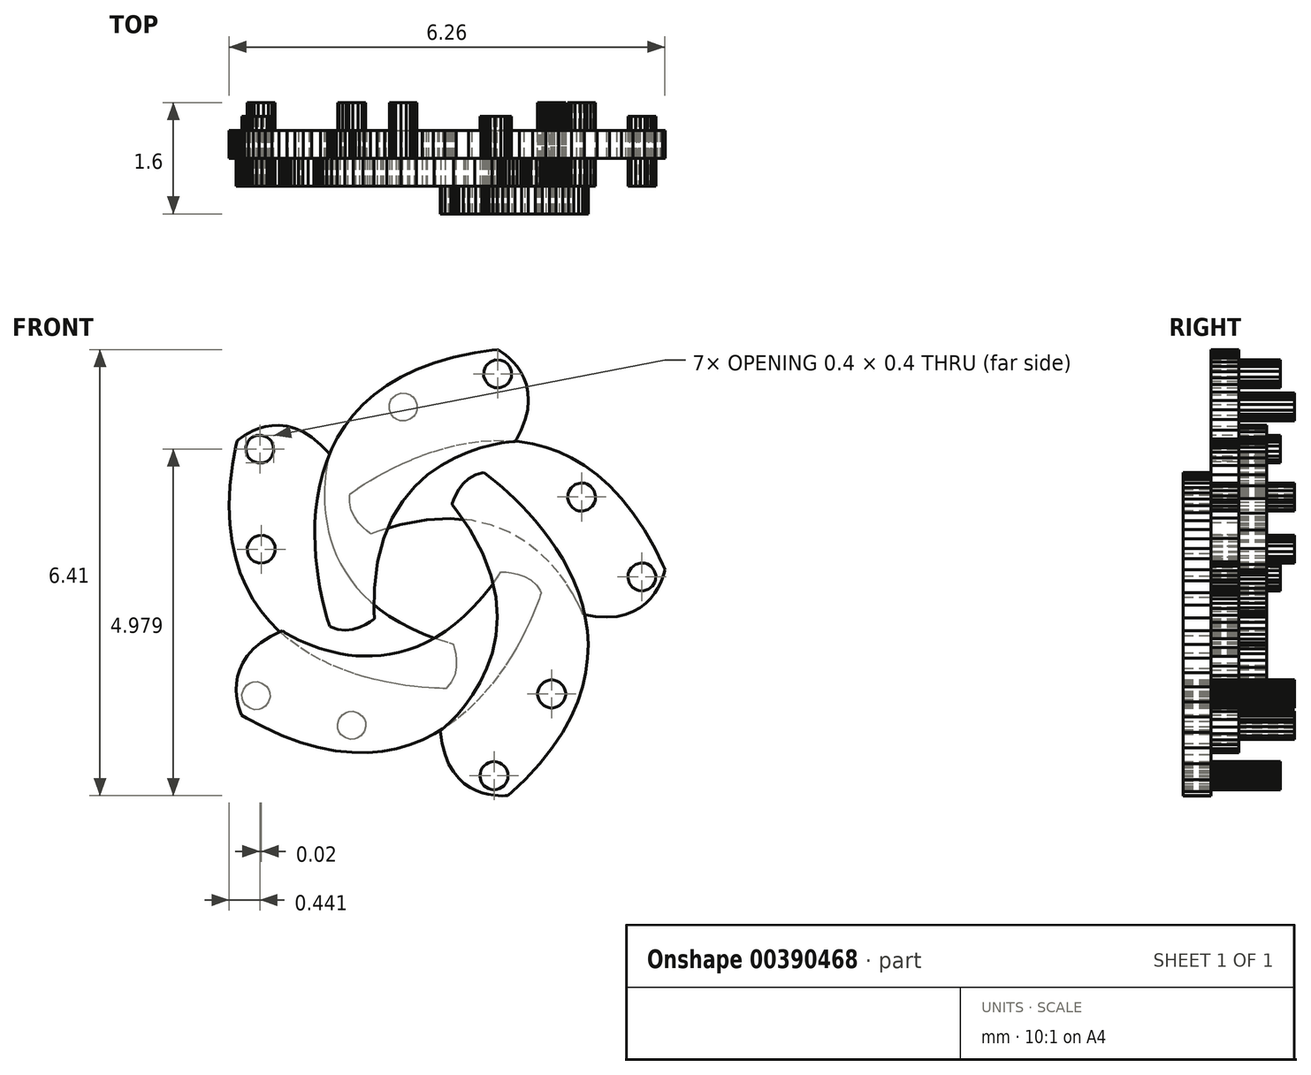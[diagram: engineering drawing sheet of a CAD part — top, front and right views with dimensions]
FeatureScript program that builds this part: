
annotation { "Feature Type Name" : "Feature", "Feature Type Description" : "" }
export const myFeature = defineFeature(function(context is Context, id is Id, definition is map)
    precondition{}
    {
        {
            var Q0;
            Q0=qCreatedBy(makeId("Front.planeOp"),FACE);
            var sketch = newSketch(context, id + "F0", { "sketchPlane" : qUnion([Q0])});
            skLineSegment(sketch, "E0", {"start": v(0.33, 0.98) * mm, "end": v(0.34, 1) * mm});
            skLineSegment(sketch, "E1", {"start": v(0.34, 1) * mm, "end": v(0.36, 1.05) * mm});
            skLineSegment(sketch, "E2", {"start": v(0.36, 1.05) * mm, "end": v(0.39, 1.12) * mm});
            skLineSegment(sketch, "E3", {"start": v(0.39, 1.12) * mm, "end": v(0.43, 1.2) * mm});
            skLineSegment(sketch, "E4", {"start": v(0.43, 1.2) * mm, "end": v(0.5, 1.28) * mm});
            skLineSegment(sketch, "E5", {"start": v(0.5, 1.28) * mm, "end": v(0.57, 1.36) * mm});
            skLineSegment(sketch, "E6", {"start": v(0.57, 1.36) * mm, "end": v(0.67, 1.41) * mm});
            skLineSegment(sketch, "E7", {"start": v(0.67, 1.41) * mm, "end": v(0.76, 1.44) * mm});
            skLineSegment(sketch, "E8", {"start": v(0.76, 1.44) * mm, "end": v(0.8, 1.44) * mm});
            skLineSegment(sketch, "E9", {"start": v(0.8, 1.44) * mm, "end": v(0.8, 1.43) * mm});
            skLineSegment(sketch, "E10", {"start": v(0.8, 1.43) * mm, "end": v(0.83, 1.42) * mm});
            skLineSegment(sketch, "E11", {"start": v(0.83, 1.42) * mm, "end": v(0.87, 1.38) * mm});
            skLineSegment(sketch, "E12", {"start": v(0.87, 1.38) * mm, "end": v(0.92, 1.34) * mm});
            skLineSegment(sketch, "E13", {"start": v(0.92, 1.34) * mm, "end": v(0.99, 1.29) * mm});
            skLineSegment(sketch, "E14", {"start": v(0.99, 1.29) * mm, "end": v(1.06, 1.22) * mm});
            skLineSegment(sketch, "E15", {"start": v(1.06, 1.22) * mm, "end": v(1.15, 1.15) * mm});
            skLineSegment(sketch, "E16", {"start": v(1.15, 1.15) * mm, "end": v(1.24, 1.06) * mm});
            skLineSegment(sketch, "E17", {"start": v(1.24, 1.06) * mm, "end": v(1.33, 0.97) * mm});
            skLineSegment(sketch, "E18", {"start": v(1.33, 0.97) * mm, "end": v(1.43, 0.86) * mm});
            skLineSegment(sketch, "E19", {"start": v(1.43, 0.86) * mm, "end": v(1.53, 0.75) * mm});
            skLineSegment(sketch, "E20", {"start": v(1.53, 0.75) * mm, "end": v(1.63, 0.62) * mm});
            skLineSegment(sketch, "E21", {"start": v(1.63, 0.62) * mm, "end": v(1.73, 0.5) * mm});
            skLineSegment(sketch, "E22", {"start": v(1.73, 0.5) * mm, "end": v(1.83, 0.35) * mm});
            skLineSegment(sketch, "E23", {"start": v(1.83, 0.35) * mm, "end": v(1.92, 0.2) * mm});
            skLineSegment(sketch, "E24", {"start": v(1.92, 0.2) * mm, "end": v(2, 0.05) * mm});
            skLineSegment(sketch, "E25", {"start": v(2, 0.05) * mm, "end": v(2.08, -0.12) * mm});
            skLineSegment(sketch, "E26", {"start": v(2.08, -0.12) * mm, "end": v(2.15, -0.29) * mm});
            skLineSegment(sketch, "E27", {"start": v(2.15, -0.29) * mm, "end": v(2.2, -0.46) * mm});
            skLineSegment(sketch, "E28", {"start": v(2.2, -0.46) * mm, "end": v(2.25, -0.64) * mm});
            skLineSegment(sketch, "E29", {"start": v(2.25, -0.64) * mm, "end": v(2.28, -0.83) * mm});
            skLineSegment(sketch, "E30", {"start": v(2.28, -0.83) * mm, "end": v(2.29, -1.03) * mm});
            skLineSegment(sketch, "E31", {"start": v(2.29, -1.03) * mm, "end": v(2.28, -1.23) * mm});
            skLineSegment(sketch, "E32", {"start": v(2.28, -1.23) * mm, "end": v(2.26, -1.43) * mm});
            skLineSegment(sketch, "E33", {"start": v(2.26, -1.43) * mm, "end": v(2.2, -1.64) * mm});
            skLineSegment(sketch, "E34", {"start": v(2.2, -1.64) * mm, "end": v(2.14, -1.85) * mm});
            skLineSegment(sketch, "E35", {"start": v(2.14, -1.85) * mm, "end": v(2.04, -2.07) * mm});
            skLineSegment(sketch, "E36", {"start": v(2.04, -2.07) * mm, "end": v(1.92, -2.29) * mm});
            skLineSegment(sketch, "E37", {"start": v(1.92, -2.29) * mm, "end": v(1.77, -2.51) * mm});
            skLineSegment(sketch, "E38", {"start": v(1.77, -2.51) * mm, "end": v(1.6, -2.74) * mm});
            skLineSegment(sketch, "E39", {"start": v(1.6, -2.74) * mm, "end": v(1.38, -2.97) * mm});
            skLineSegment(sketch, "E40", {"start": v(1.38, -2.97) * mm, "end": v(1.2, -3.14) * mm});
            skLineSegment(sketch, "E41", {"start": v(1.2, -3.14) * mm, "end": v(1.14, -3.2) * mm});
            skLineSegment(sketch, "E42", {"start": v(1.14, -3.2) * mm, "end": v(1.13, -3.2) * mm});
            skLineSegment(sketch, "E43", {"start": v(1.13, -3.2) * mm, "end": v(1.1, -3.2) * mm});
            skLineSegment(sketch, "E44", {"start": v(1.1, -3.2) * mm, "end": v(1.06, -3.2) * mm});
            skLineSegment(sketch, "E45", {"start": v(1.06, -3.2) * mm, "end": v(1, -3.2) * mm});
            skLineSegment(sketch, "E46", {"start": v(1, -3.2) * mm, "end": v(0.93, -3.2) * mm});
            skLineSegment(sketch, "E47", {"start": v(0.93, -3.2) * mm, "end": v(0.85, -3.18) * mm});
            skLineSegment(sketch, "E48", {"start": v(0.85, -3.18) * mm, "end": v(0.77, -3.16) * mm});
            skLineSegment(sketch, "E49", {"start": v(0.77, -3.16) * mm, "end": v(0.68, -3.13) * mm});
            skLineSegment(sketch, "E50", {"start": v(0.68, -3.13) * mm, "end": v(0.6, -3.09) * mm});
            skLineSegment(sketch, "E51", {"start": v(0.6, -3.09) * mm, "end": v(0.51, -3.03) * mm});
            skLineSegment(sketch, "E52", {"start": v(0.51, -3.03) * mm, "end": v(0.43, -2.95) * mm});
            skLineSegment(sketch, "E53", {"start": v(0.43, -2.95) * mm, "end": v(0.35, -2.86) * mm});
            skLineSegment(sketch, "E54", {"start": v(0.35, -2.86) * mm, "end": v(0.29, -2.75) * mm});
            skLineSegment(sketch, "E55", {"start": v(0.29, -2.75) * mm, "end": v(0.23, -2.61) * mm});
            skLineSegment(sketch, "E56", {"start": v(0.23, -2.61) * mm, "end": v(0.2, -2.45) * mm});
            skLineSegment(sketch, "E57", {"start": v(0.2, -2.45) * mm, "end": v(0.17, -2.31) * mm});
            skLineSegment(sketch, "E58", {"start": v(0.17, -2.31) * mm, "end": v(0.17, -2.27) * mm});
            skLineSegment(sketch, "E59", {"start": v(0.17, -2.27) * mm, "end": v(0.19, -2.25) * mm});
            skLineSegment(sketch, "E60", {"start": v(0.19, -2.25) * mm, "end": v(0.24, -2.2) * mm});
            skLineSegment(sketch, "E61", {"start": v(0.24, -2.2) * mm, "end": v(0.32, -2.14) * mm});
            skLineSegment(sketch, "E62", {"start": v(0.32, -2.14) * mm, "end": v(0.41, -2.03) * mm});
            skLineSegment(sketch, "E63", {"start": v(0.41, -2.03) * mm, "end": v(0.52, -1.9) * mm});
            skLineSegment(sketch, "E64", {"start": v(0.52, -1.9) * mm, "end": v(0.63, -1.75) * mm});
            skLineSegment(sketch, "E65", {"start": v(0.63, -1.75) * mm, "end": v(0.74, -1.57) * mm});
            skLineSegment(sketch, "E66", {"start": v(0.74, -1.57) * mm, "end": v(0.83, -1.37) * mm});
            skLineSegment(sketch, "E67", {"start": v(0.83, -1.37) * mm, "end": v(0.91, -1.15) * mm});
            skLineSegment(sketch, "E68", {"start": v(0.91, -1.15) * mm, "end": v(0.96, -0.9) * mm});
            skLineSegment(sketch, "E69", {"start": v(0.96, -0.9) * mm, "end": v(0.98, -0.63) * mm});
            skLineSegment(sketch, "E70", {"start": v(0.98, -0.63) * mm, "end": v(0.96, -0.35) * mm});
            skLineSegment(sketch, "E71", {"start": v(0.96, -0.35) * mm, "end": v(0.9, -0.04) * mm});
            skLineSegment(sketch, "E72", {"start": v(0.9, -0.04) * mm, "end": v(0.77, 0.28) * mm});
            skLineSegment(sketch, "E73", {"start": v(0.77, 0.28) * mm, "end": v(0.59, 0.62) * mm});
            skLineSegment(sketch, "E74", {"start": v(0.59, 0.62) * mm, "end": v(0.4, 0.9) * mm});
            skLineSegment(sketch, "E75", {"start": v(0.4, 0.9) * mm, "end": v(0.33, 0.98) * mm});
            skLineSegment(sketch, "E76", {"start": v(1.14, -2.91) * mm, "end": v(1.14, -2.92) * mm});
            skLineSegment(sketch, "E77", {"start": v(1.14, -2.92) * mm, "end": v(1.13, -2.95) * mm});
            skLineSegment(sketch, "E78", {"start": v(1.13, -2.95) * mm, "end": v(1.12, -3) * mm});
            skLineSegment(sketch, "E79", {"start": v(1.12, -3) * mm, "end": v(1.1, -3.03) * mm});
            skLineSegment(sketch, "E80", {"start": v(1.1, -3.03) * mm, "end": v(1.08, -3.06) * mm});
            skLineSegment(sketch, "E81", {"start": v(1.08, -3.06) * mm, "end": v(1.05, -3.08) * mm});
            skLineSegment(sketch, "E82", {"start": v(1.05, -3.08) * mm, "end": v(1.02, -3.1) * mm});
            skLineSegment(sketch, "E83", {"start": v(1.02, -3.1) * mm, "end": v(0.98, -3.11) * mm});
            skLineSegment(sketch, "E84", {"start": v(0.98, -3.11) * mm, "end": v(0.95, -3.12) * mm});
            skLineSegment(sketch, "E85", {"start": v(0.95, -3.12) * mm, "end": v(0.94, -3.12) * mm});
            skLineSegment(sketch, "E86", {"start": v(0.94, -3.12) * mm, "end": v(0.93, -3.12) * mm});
            skLineSegment(sketch, "E87", {"start": v(0.93, -3.12) * mm, "end": v(0.9, -3.11) * mm});
            skLineSegment(sketch, "E88", {"start": v(0.9, -3.11) * mm, "end": v(0.86, -3.1) * mm});
            skLineSegment(sketch, "E89", {"start": v(0.86, -3.1) * mm, "end": v(0.82, -3.08) * mm});
            skLineSegment(sketch, "E90", {"start": v(0.82, -3.08) * mm, "end": v(0.8, -3.06) * mm});
            skLineSegment(sketch, "E91", {"start": v(0.8, -3.06) * mm, "end": v(0.77, -3.03) * mm});
            skLineSegment(sketch, "E92", {"start": v(0.77, -3.03) * mm, "end": v(0.75, -3) * mm});
            skLineSegment(sketch, "E93", {"start": v(0.75, -3) * mm, "end": v(0.74, -2.95) * mm});
            skLineSegment(sketch, "E94", {"start": v(0.74, -2.95) * mm, "end": v(0.74, -2.92) * mm});
            skLineSegment(sketch, "E95", {"start": v(0.74, -2.92) * mm, "end": v(0.74, -2.91) * mm});
            skLineSegment(sketch, "E96", {"start": v(0.74, -2.91) * mm, "end": v(0.74, -2.9) * mm});
            skLineSegment(sketch, "E97", {"start": v(0.74, -2.9) * mm, "end": v(0.74, -2.87) * mm});
            skLineSegment(sketch, "E98", {"start": v(0.74, -2.87) * mm, "end": v(0.75, -2.84) * mm});
            skLineSegment(sketch, "E99", {"start": v(0.75, -2.84) * mm, "end": v(0.77, -2.8) * mm});
            skLineSegment(sketch, "E100", {"start": v(0.77, -2.8) * mm, "end": v(0.8, -2.77) * mm});
            skLineSegment(sketch, "E101", {"start": v(0.8, -2.77) * mm, "end": v(0.82, -2.75) * mm});
            skLineSegment(sketch, "E102", {"start": v(0.82, -2.75) * mm, "end": v(0.86, -2.73) * mm});
            skLineSegment(sketch, "E103", {"start": v(0.86, -2.73) * mm, "end": v(0.9, -2.72) * mm});
            skLineSegment(sketch, "E104", {"start": v(0.9, -2.72) * mm, "end": v(0.93, -2.71) * mm});
            skLineSegment(sketch, "E105", {"start": v(0.93, -2.71) * mm, "end": v(0.94, -2.71) * mm});
            skLineSegment(sketch, "E106", {"start": v(0.94, -2.71) * mm, "end": v(0.95, -2.71) * mm});
            skLineSegment(sketch, "E107", {"start": v(0.95, -2.71) * mm, "end": v(0.98, -2.72) * mm});
            skLineSegment(sketch, "E108", {"start": v(0.98, -2.72) * mm, "end": v(1.02, -2.73) * mm});
            skLineSegment(sketch, "E109", {"start": v(1.02, -2.73) * mm, "end": v(1.05, -2.75) * mm});
            skLineSegment(sketch, "E110", {"start": v(1.05, -2.75) * mm, "end": v(1.08, -2.77) * mm});
            skLineSegment(sketch, "E111", {"start": v(1.08, -2.77) * mm, "end": v(1.1, -2.8) * mm});
            skLineSegment(sketch, "E112", {"start": v(1.1, -2.8) * mm, "end": v(1.12, -2.84) * mm});
            skLineSegment(sketch, "E113", {"start": v(1.12, -2.84) * mm, "end": v(1.13, -2.87) * mm});
            skLineSegment(sketch, "E114", {"start": v(1.13, -2.87) * mm, "end": v(1.14, -2.9) * mm});
            skLineSegment(sketch, "E115", {"start": v(1.14, -2.9) * mm, "end": v(1.14, -2.91) * mm});
            skLineSegment(sketch, "E116", {"start": v(1.97, -1.74) * mm, "end": v(1.97, -1.75) * mm});
            skLineSegment(sketch, "E117", {"start": v(1.97, -1.75) * mm, "end": v(1.96, -1.78) * mm});
            skLineSegment(sketch, "E118", {"start": v(1.96, -1.78) * mm, "end": v(1.95, -1.82) * mm});
            skLineSegment(sketch, "E119", {"start": v(1.95, -1.82) * mm, "end": v(1.93, -1.85) * mm});
            skLineSegment(sketch, "E120", {"start": v(1.93, -1.85) * mm, "end": v(1.9, -1.88) * mm});
            skLineSegment(sketch, "E121", {"start": v(1.9, -1.88) * mm, "end": v(1.88, -1.9) * mm});
            skLineSegment(sketch, "E122", {"start": v(1.88, -1.9) * mm, "end": v(1.84, -1.92) * mm});
            skLineSegment(sketch, "E123", {"start": v(1.84, -1.92) * mm, "end": v(1.8, -1.94) * mm});
            skLineSegment(sketch, "E124", {"start": v(1.8, -1.94) * mm, "end": v(1.78, -1.94) * mm});
            skLineSegment(sketch, "E125", {"start": v(1.78, -1.94) * mm, "end": v(1.77, -1.94) * mm});
            skLineSegment(sketch, "E126", {"start": v(1.77, -1.94) * mm, "end": v(1.76, -1.94) * mm});
            skLineSegment(sketch, "E127", {"start": v(1.76, -1.94) * mm, "end": v(1.72, -1.94) * mm});
            skLineSegment(sketch, "E128", {"start": v(1.72, -1.94) * mm, "end": v(1.69, -1.92) * mm});
            skLineSegment(sketch, "E129", {"start": v(1.69, -1.92) * mm, "end": v(1.65, -1.9) * mm});
            skLineSegment(sketch, "E130", {"start": v(1.65, -1.9) * mm, "end": v(1.62, -1.88) * mm});
            skLineSegment(sketch, "E131", {"start": v(1.62, -1.88) * mm, "end": v(1.6, -1.85) * mm});
            skLineSegment(sketch, "E132", {"start": v(1.6, -1.85) * mm, "end": v(1.58, -1.82) * mm});
            skLineSegment(sketch, "E133", {"start": v(1.58, -1.82) * mm, "end": v(1.57, -1.78) * mm});
            skLineSegment(sketch, "E134", {"start": v(1.57, -1.78) * mm, "end": v(1.56, -1.75) * mm});
            skLineSegment(sketch, "E135", {"start": v(1.56, -1.75) * mm, "end": v(1.56, -1.74) * mm});
            skLineSegment(sketch, "E136", {"start": v(1.56, -1.74) * mm, "end": v(1.56, -1.73) * mm});
            skLineSegment(sketch, "E137", {"start": v(1.56, -1.73) * mm, "end": v(1.57, -1.7) * mm});
            skLineSegment(sketch, "E138", {"start": v(1.57, -1.7) * mm, "end": v(1.58, -1.66) * mm});
            skLineSegment(sketch, "E139", {"start": v(1.58, -1.66) * mm, "end": v(1.6, -1.63) * mm});
            skLineSegment(sketch, "E140", {"start": v(1.6, -1.63) * mm, "end": v(1.62, -1.6) * mm});
            skLineSegment(sketch, "E141", {"start": v(1.62, -1.6) * mm, "end": v(1.65, -1.57) * mm});
            skLineSegment(sketch, "E142", {"start": v(1.65, -1.57) * mm, "end": v(1.69, -1.55) * mm});
            skLineSegment(sketch, "E143", {"start": v(1.69, -1.55) * mm, "end": v(1.72, -1.54) * mm});
            skLineSegment(sketch, "E144", {"start": v(1.72, -1.54) * mm, "end": v(1.76, -1.54) * mm});
            skLineSegment(sketch, "E145", {"start": v(1.76, -1.54) * mm, "end": v(1.77, -1.54) * mm});
            skLineSegment(sketch, "E146", {"start": v(1.77, -1.54) * mm, "end": v(1.78, -1.54) * mm});
            skLineSegment(sketch, "E147", {"start": v(1.78, -1.54) * mm, "end": v(1.8, -1.54) * mm});
            skLineSegment(sketch, "E148", {"start": v(1.8, -1.54) * mm, "end": v(1.84, -1.55) * mm});
            skLineSegment(sketch, "E149", {"start": v(1.84, -1.55) * mm, "end": v(1.88, -1.57) * mm});
            skLineSegment(sketch, "E150", {"start": v(1.88, -1.57) * mm, "end": v(1.9, -1.6) * mm});
            skLineSegment(sketch, "E151", {"start": v(1.9, -1.6) * mm, "end": v(1.93, -1.63) * mm});
            skLineSegment(sketch, "E152", {"start": v(1.93, -1.63) * mm, "end": v(1.95, -1.66) * mm});
            skLineSegment(sketch, "E153", {"start": v(1.95, -1.66) * mm, "end": v(1.96, -1.7) * mm});
            skLineSegment(sketch, "E154", {"start": v(1.96, -1.7) * mm, "end": v(1.97, -1.73) * mm});
            skLineSegment(sketch, "E155", {"start": v(1.97, -1.73) * mm, "end": v(1.97, -1.74) * mm});
            skLineSegment(sketch, "E156", {"start": v(-0.83, 0.56) * mm, "end": v(-0.85, 0.57) * mm});
            skLineSegment(sketch, "E157", {"start": v(-0.85, 0.57) * mm, "end": v(-0.89, 0.6) * mm});
            skLineSegment(sketch, "E158", {"start": v(-0.89, 0.6) * mm, "end": v(-0.95, 0.65) * mm});
            skLineSegment(sketch, "E159", {"start": v(-0.95, 0.65) * mm, "end": v(-1, 0.72) * mm});
            skLineSegment(sketch, "E160", {"start": v(-1, 0.72) * mm, "end": v(-1.07, 0.8) * mm});
            skLineSegment(sketch, "E161", {"start": v(-1.07, 0.8) * mm, "end": v(-1.12, 0.9) * mm});
            skLineSegment(sketch, "E162", {"start": v(-1.12, 0.9) * mm, "end": v(-1.14, 1.02) * mm});
            skLineSegment(sketch, "E163", {"start": v(-1.14, 1.02) * mm, "end": v(-1.13, 1.1) * mm});
            skLineSegment(sketch, "E164", {"start": v(-1.13, 1.1) * mm, "end": v(-1.13, 1.14) * mm});
            skLineSegment(sketch, "E165", {"start": v(-1.13, 1.14) * mm, "end": v(-1.12, 1.14) * mm});
            skLineSegment(sketch, "E166", {"start": v(-1.12, 1.14) * mm, "end": v(-1.1, 1.16) * mm});
            skLineSegment(sketch, "E167", {"start": v(-1.1, 1.16) * mm, "end": v(-1.05, 1.2) * mm});
            skLineSegment(sketch, "E168", {"start": v(-1.05, 1.2) * mm, "end": v(-1, 1.23) * mm});
            skLineSegment(sketch, "E169", {"start": v(-1, 1.23) * mm, "end": v(-0.92, 1.28) * mm});
            skLineSegment(sketch, "E170", {"start": v(-0.92, 1.28) * mm, "end": v(-0.84, 1.33) * mm});
            skLineSegment(sketch, "E171", {"start": v(-0.84, 1.33) * mm, "end": v(-0.74, 1.39) * mm});
            skLineSegment(sketch, "E172", {"start": v(-0.74, 1.39) * mm, "end": v(-0.63, 1.45) * mm});
            skLineSegment(sketch, "E173", {"start": v(-0.63, 1.45) * mm, "end": v(-0.51, 1.5) * mm});
            skLineSegment(sketch, "E174", {"start": v(-0.51, 1.5) * mm, "end": v(-0.38, 1.57) * mm});
            skLineSegment(sketch, "E175", {"start": v(-0.38, 1.57) * mm, "end": v(-0.24, 1.63) * mm});
            skLineSegment(sketch, "E176", {"start": v(-0.24, 1.63) * mm, "end": v(-0.1, 1.69) * mm});
            skLineSegment(sketch, "E177", {"start": v(-0.1, 1.69) * mm, "end": v(0.06, 1.74) * mm});
            skLineSegment(sketch, "E178", {"start": v(0.06, 1.74) * mm, "end": v(0.23, 1.8) * mm});
            skLineSegment(sketch, "E179", {"start": v(0.23, 1.8) * mm, "end": v(0.4, 1.83) * mm});
            skLineSegment(sketch, "E180", {"start": v(0.4, 1.83) * mm, "end": v(0.57, 1.87) * mm});
            skLineSegment(sketch, "E181", {"start": v(0.57, 1.87) * mm, "end": v(0.75, 1.9) * mm});
            skLineSegment(sketch, "E182", {"start": v(0.75, 1.9) * mm, "end": v(0.93, 1.9) * mm});
            skLineSegment(sketch, "E183", {"start": v(0.93, 1.9) * mm, "end": v(1.12, 1.9) * mm});
            skLineSegment(sketch, "E184", {"start": v(1.12, 1.9) * mm, "end": v(1.3, 1.89) * mm});
            skLineSegment(sketch, "E185", {"start": v(1.3, 1.89) * mm, "end": v(1.5, 1.86) * mm});
            skLineSegment(sketch, "E186", {"start": v(1.5, 1.86) * mm, "end": v(1.68, 1.8) * mm});
            skLineSegment(sketch, "E187", {"start": v(1.68, 1.8) * mm, "end": v(1.87, 1.74) * mm});
            skLineSegment(sketch, "E188", {"start": v(1.87, 1.74) * mm, "end": v(2.05, 1.65) * mm});
            skLineSegment(sketch, "E189", {"start": v(2.05, 1.65) * mm, "end": v(2.24, 1.54) * mm});
            skLineSegment(sketch, "E190", {"start": v(2.24, 1.54) * mm, "end": v(2.42, 1.41) * mm});
            skLineSegment(sketch, "E191", {"start": v(2.42, 1.41) * mm, "end": v(2.6, 1.25) * mm});
            skLineSegment(sketch, "E192", {"start": v(2.6, 1.25) * mm, "end": v(2.77, 1.07) * mm});
            skLineSegment(sketch, "E193", {"start": v(2.77, 1.07) * mm, "end": v(2.94, 0.86) * mm});
            skLineSegment(sketch, "E194", {"start": v(2.94, 0.86) * mm, "end": v(3.1, 0.62) * mm});
            skLineSegment(sketch, "E195", {"start": v(3.1, 0.62) * mm, "end": v(3.25, 0.35) * mm});
            skLineSegment(sketch, "E196", {"start": v(3.25, 0.35) * mm, "end": v(3.36, 0.12) * mm});
            skLineSegment(sketch, "E197", {"start": v(3.36, 0.12) * mm, "end": v(3.4, 0.05) * mm});
            skLineSegment(sketch, "E198", {"start": v(3.4, 0.05) * mm, "end": v(3.4, 0.04) * mm});
            skLineSegment(sketch, "E199", {"start": v(3.4, 0.04) * mm, "end": v(3.39, 0) * mm});
            skLineSegment(sketch, "E200", {"start": v(3.39, 0) * mm, "end": v(3.37, -0.03) * mm});
            skLineSegment(sketch, "E201", {"start": v(3.37, -0.03) * mm, "end": v(3.35, -0.09) * mm});
            skLineSegment(sketch, "E202", {"start": v(3.35, -0.09) * mm, "end": v(3.33, -0.15) * mm});
            skLineSegment(sketch, "E203", {"start": v(3.33, -0.15) * mm, "end": v(3.3, -0.22) * mm});
            skLineSegment(sketch, "E204", {"start": v(3.3, -0.22) * mm, "end": v(3.25, -0.3) * mm});
            skLineSegment(sketch, "E205", {"start": v(3.25, -0.3) * mm, "end": v(3.19, -0.36) * mm});
            skLineSegment(sketch, "E206", {"start": v(3.19, -0.36) * mm, "end": v(3.12, -0.43) * mm});
            skLineSegment(sketch, "E207", {"start": v(3.12, -0.43) * mm, "end": v(3.04, -0.5) * mm});
            skLineSegment(sketch, "E208", {"start": v(3.04, -0.5) * mm, "end": v(2.94, -0.55) * mm});
            skLineSegment(sketch, "E209", {"start": v(2.94, -0.55) * mm, "end": v(2.83, -0.6) * mm});
            skLineSegment(sketch, "E210", {"start": v(2.83, -0.6) * mm, "end": v(2.7, -0.62) * mm});
            skLineSegment(sketch, "E211", {"start": v(2.7, -0.62) * mm, "end": v(2.56, -0.64) * mm});
            skLineSegment(sketch, "E212", {"start": v(2.56, -0.64) * mm, "end": v(2.4, -0.63) * mm});
            skLineSegment(sketch, "E213", {"start": v(2.4, -0.63) * mm, "end": v(2.26, -0.6) * mm});
            skLineSegment(sketch, "E214", {"start": v(2.26, -0.6) * mm, "end": v(2.21, -0.6) * mm});
            skLineSegment(sketch, "E215", {"start": v(2.21, -0.6) * mm, "end": v(2.2, -0.57) * mm});
            skLineSegment(sketch, "E216", {"start": v(2.2, -0.57) * mm, "end": v(2.18, -0.5) * mm});
            skLineSegment(sketch, "E217", {"start": v(2.18, -0.5) * mm, "end": v(2.13, -0.41) * mm});
            skLineSegment(sketch, "E218", {"start": v(2.13, -0.41) * mm, "end": v(2.06, -0.29) * mm});
            skLineSegment(sketch, "E219", {"start": v(2.06, -0.29) * mm, "end": v(1.97, -0.15) * mm});
            skLineSegment(sketch, "E220", {"start": v(1.97, -0.15) * mm, "end": v(1.86, 0) * mm});
            skLineSegment(sketch, "E221", {"start": v(1.86, 0) * mm, "end": v(1.72, 0.16) * mm});
            skLineSegment(sketch, "E222", {"start": v(1.72, 0.16) * mm, "end": v(1.56, 0.32) * mm});
            skLineSegment(sketch, "E223", {"start": v(1.56, 0.32) * mm, "end": v(1.37, 0.46) * mm});
            skLineSegment(sketch, "E224", {"start": v(1.37, 0.46) * mm, "end": v(1.15, 0.58) * mm});
            skLineSegment(sketch, "E225", {"start": v(1.15, 0.58) * mm, "end": v(0.9, 0.69) * mm});
            skLineSegment(sketch, "E226", {"start": v(0.9, 0.69) * mm, "end": v(0.63, 0.75) * mm});
            skLineSegment(sketch, "E227", {"start": v(0.63, 0.75) * mm, "end": v(0.31, 0.78) * mm});
            skLineSegment(sketch, "E228", {"start": v(0.31, 0.78) * mm, "end": v(-0.03, 0.77) * mm});
            skLineSegment(sketch, "E229", {"start": v(-0.03, 0.77) * mm, "end": v(-0.41, 0.7) * mm});
            skLineSegment(sketch, "E230", {"start": v(-0.41, 0.7) * mm, "end": v(-0.73, 0.6) * mm});
            skLineSegment(sketch, "E231", {"start": v(-0.73, 0.6) * mm, "end": v(-0.83, 0.56) * mm});
            skLineSegment(sketch, "E232", {"start": v(3.12, 0.13) * mm, "end": v(3.14, 0.13) * mm});
            skLineSegment(sketch, "E233", {"start": v(3.14, 0.13) * mm, "end": v(3.2, 0.1) * mm});
            skLineSegment(sketch, "E234", {"start": v(3.2, 0.1) * mm, "end": v(3.24, 0.03) * mm});
            skLineSegment(sketch, "E235", {"start": v(3.24, 0.03) * mm, "end": v(3.26, -0.04) * mm});
            skLineSegment(sketch, "E236", {"start": v(3.26, -0.04) * mm, "end": v(3.26, -0.1) * mm});
            skLineSegment(sketch, "E237", {"start": v(3.26, -0.1) * mm, "end": v(3.25, -0.12) * mm});
            skLineSegment(sketch, "E238", {"start": v(3.25, -0.12) * mm, "end": v(3.25, -0.14) * mm});
            skLineSegment(sketch, "E239", {"start": v(3.25, -0.14) * mm, "end": v(3.21, -0.19) * mm});
            skLineSegment(sketch, "E240", {"start": v(3.21, -0.19) * mm, "end": v(3.15, -0.24) * mm});
            skLineSegment(sketch, "E241", {"start": v(3.15, -0.24) * mm, "end": v(3.08, -0.26) * mm});
            skLineSegment(sketch, "E242", {"start": v(3.08, -0.26) * mm, "end": v(3.02, -0.26) * mm});
            skLineSegment(sketch, "E243", {"start": v(3.02, -0.26) * mm, "end": v(3, -0.25) * mm});
            skLineSegment(sketch, "E244", {"start": v(3, -0.25) * mm, "end": v(2.98, -0.24) * mm});
            skLineSegment(sketch, "E245", {"start": v(2.98, -0.24) * mm, "end": v(2.93, -0.21) * mm});
            skLineSegment(sketch, "E246", {"start": v(2.93, -0.21) * mm, "end": v(2.88, -0.15) * mm});
            skLineSegment(sketch, "E247", {"start": v(2.88, -0.15) * mm, "end": v(2.86, -0.08) * mm});
            skLineSegment(sketch, "E248", {"start": v(2.86, -0.08) * mm, "end": v(2.86, -0.01) * mm});
            skLineSegment(sketch, "E249", {"start": v(2.86, -0.01) * mm, "end": v(2.87, 0) * mm});
            skLineSegment(sketch, "E250", {"start": v(2.87, 0) * mm, "end": v(2.88, 0.02) * mm});
            skLineSegment(sketch, "E251", {"start": v(2.88, 0.02) * mm, "end": v(2.9, 0.07) * mm});
            skLineSegment(sketch, "E252", {"start": v(2.9, 0.07) * mm, "end": v(2.97, 0.12) * mm});
            skLineSegment(sketch, "E253", {"start": v(2.97, 0.12) * mm, "end": v(3.04, 0.14) * mm});
            skLineSegment(sketch, "E254", {"start": v(3.04, 0.14) * mm, "end": v(3.1, 0.14) * mm});
            skLineSegment(sketch, "E255", {"start": v(3.1, 0.14) * mm, "end": v(3.12, 0.13) * mm});
            skLineSegment(sketch, "E256", {"start": v(2.26, 1.28) * mm, "end": v(2.28, 1.28) * mm});
            skLineSegment(sketch, "E257", {"start": v(2.28, 1.28) * mm, "end": v(2.33, 1.24) * mm});
            skLineSegment(sketch, "E258", {"start": v(2.33, 1.24) * mm, "end": v(2.37, 1.18) * mm});
            skLineSegment(sketch, "E259", {"start": v(2.37, 1.18) * mm, "end": v(2.4, 1.1) * mm});
            skLineSegment(sketch, "E260", {"start": v(2.4, 1.1) * mm, "end": v(2.4, 1.05) * mm});
            skLineSegment(sketch, "E261", {"start": v(2.4, 1.05) * mm, "end": v(2.39, 1.03) * mm});
            skLineSegment(sketch, "E262", {"start": v(2.39, 1.03) * mm, "end": v(2.38, 1.01) * mm});
            skLineSegment(sketch, "E263", {"start": v(2.38, 1.01) * mm, "end": v(2.35, 0.96) * mm});
            skLineSegment(sketch, "E264", {"start": v(2.35, 0.96) * mm, "end": v(2.29, 0.91) * mm});
            skLineSegment(sketch, "E265", {"start": v(2.29, 0.91) * mm, "end": v(2.21, 0.9) * mm});
            skLineSegment(sketch, "E266", {"start": v(2.21, 0.9) * mm, "end": v(2.15, 0.9) * mm});
            skLineSegment(sketch, "E267", {"start": v(2.15, 0.9) * mm, "end": v(2.13, 0.9) * mm});
            skLineSegment(sketch, "E268", {"start": v(2.13, 0.9) * mm, "end": v(2.12, 0.9) * mm});
            skLineSegment(sketch, "E269", {"start": v(2.12, 0.9) * mm, "end": v(2.06, 0.94) * mm});
            skLineSegment(sketch, "E270", {"start": v(2.06, 0.94) * mm, "end": v(2.02, 1) * mm});
            skLineSegment(sketch, "E271", {"start": v(2.02, 1) * mm, "end": v(2, 1.07) * mm});
            skLineSegment(sketch, "E272", {"start": v(2, 1.07) * mm, "end": v(2, 1.13) * mm});
            skLineSegment(sketch, "E273", {"start": v(2, 1.13) * mm, "end": v(2, 1.15) * mm});
            skLineSegment(sketch, "E274", {"start": v(2, 1.15) * mm, "end": v(2, 1.17) * mm});
            skLineSegment(sketch, "E275", {"start": v(2, 1.17) * mm, "end": v(2.04, 1.22) * mm});
            skLineSegment(sketch, "E276", {"start": v(2.04, 1.22) * mm, "end": v(2.1, 1.27) * mm});
            skLineSegment(sketch, "E277", {"start": v(2.1, 1.27) * mm, "end": v(2.18, 1.3) * mm});
            skLineSegment(sketch, "E278", {"start": v(2.18, 1.3) * mm, "end": v(2.24, 1.29) * mm});
            skLineSegment(sketch, "E279", {"start": v(2.24, 1.29) * mm, "end": v(2.26, 1.28) * mm});
            skLineSegment(sketch, "E280", {"start": v(-0.78, -0.66) * mm, "end": v(-0.8, -0.67) * mm});
            skLineSegment(sketch, "E281", {"start": v(-0.8, -0.67) * mm, "end": v(-0.84, -0.7) * mm});
            skLineSegment(sketch, "E282", {"start": v(-0.84, -0.7) * mm, "end": v(-0.9, -0.74) * mm});
            skLineSegment(sketch, "E283", {"start": v(-0.9, -0.74) * mm, "end": v(-1, -0.78) * mm});
            skLineSegment(sketch, "E284", {"start": v(-1, -0.78) * mm, "end": v(-1.09, -0.81) * mm});
            skLineSegment(sketch, "E285", {"start": v(-1.09, -0.81) * mm, "end": v(-1.2, -0.83) * mm});
            skLineSegment(sketch, "E286", {"start": v(-1.2, -0.83) * mm, "end": v(-1.3, -0.81) * mm});
            skLineSegment(sketch, "E287", {"start": v(-1.3, -0.81) * mm, "end": v(-1.4, -0.78) * mm});
            skLineSegment(sketch, "E288", {"start": v(-1.4, -0.78) * mm, "end": v(-1.42, -0.77) * mm});
            skLineSegment(sketch, "E289", {"start": v(-1.42, -0.77) * mm, "end": v(-1.43, -0.76) * mm});
            skLineSegment(sketch, "E290", {"start": v(-1.43, -0.76) * mm, "end": v(-1.44, -0.73) * mm});
            skLineSegment(sketch, "E291", {"start": v(-1.44, -0.73) * mm, "end": v(-1.45, -0.68) * mm});
            skLineSegment(sketch, "E292", {"start": v(-1.45, -0.68) * mm, "end": v(-1.47, -0.61) * mm});
            skLineSegment(sketch, "E293", {"start": v(-1.47, -0.61) * mm, "end": v(-1.5, -0.53) * mm});
            skLineSegment(sketch, "E294", {"start": v(-1.5, -0.53) * mm, "end": v(-1.52, -0.43) * mm});
            skLineSegment(sketch, "E295", {"start": v(-1.52, -0.43) * mm, "end": v(-1.54, -0.32) * mm});
            skLineSegment(sketch, "E296", {"start": v(-1.54, -0.32) * mm, "end": v(-1.57, -0.2) * mm});
            skLineSegment(sketch, "E297", {"start": v(-1.57, -0.2) * mm, "end": v(-1.59, -0.07) * mm});
            skLineSegment(sketch, "E298", {"start": v(-1.59, -0.07) * mm, "end": v(-1.6, 0.08) * mm});
            skLineSegment(sketch, "E299", {"start": v(-1.6, 0.08) * mm, "end": v(-1.62, 0.23) * mm});
            skLineSegment(sketch, "E300", {"start": v(-1.62, 0.23) * mm, "end": v(-1.63, 0.39) * mm});
            skLineSegment(sketch, "E301", {"start": v(-1.63, 0.39) * mm, "end": v(-1.64, 0.55) * mm});
            skLineSegment(sketch, "E302", {"start": v(-1.64, 0.55) * mm, "end": v(-1.64, 0.72) * mm});
            skLineSegment(sketch, "E303", {"start": v(-1.64, 0.72) * mm, "end": v(-1.62, 0.9) * mm});
            skLineSegment(sketch, "E304", {"start": v(-1.62, 0.9) * mm, "end": v(-1.6, 1.07) * mm});
            skLineSegment(sketch, "E305", {"start": v(-1.6, 1.07) * mm, "end": v(-1.57, 1.25) * mm});
            skLineSegment(sketch, "E306", {"start": v(-1.57, 1.25) * mm, "end": v(-1.53, 1.43) * mm});
            skLineSegment(sketch, "E307", {"start": v(-1.53, 1.43) * mm, "end": v(-1.47, 1.6) * mm});
            skLineSegment(sketch, "E308", {"start": v(-1.47, 1.6) * mm, "end": v(-1.4, 1.78) * mm});
            skLineSegment(sketch, "E309", {"start": v(-1.4, 1.78) * mm, "end": v(-1.31, 1.95) * mm});
            skLineSegment(sketch, "E310", {"start": v(-1.31, 1.95) * mm, "end": v(-1.2, 2.11) * mm});
            skLineSegment(sketch, "E311", {"start": v(-1.2, 2.11) * mm, "end": v(-1.09, 2.27) * mm});
            skLineSegment(sketch, "E312", {"start": v(-1.09, 2.27) * mm, "end": v(-0.95, 2.42) * mm});
            skLineSegment(sketch, "E313", {"start": v(-0.95, 2.42) * mm, "end": v(-0.79, 2.56) * mm});
            skLineSegment(sketch, "E314", {"start": v(-0.79, 2.56) * mm, "end": v(-0.6, 2.7) * mm});
            skLineSegment(sketch, "E315", {"start": v(-0.6, 2.7) * mm, "end": v(-0.4, 2.82) * mm});
            skLineSegment(sketch, "E316", {"start": v(-0.4, 2.82) * mm, "end": v(-0.18, 2.92) * mm});
            skLineSegment(sketch, "E317", {"start": v(-0.18, 2.92) * mm, "end": v(0.08, 3.02) * mm});
            skLineSegment(sketch, "E318", {"start": v(0.08, 3.02) * mm, "end": v(0.35, 3.1) * mm});
            skLineSegment(sketch, "E319", {"start": v(0.35, 3.1) * mm, "end": v(0.66, 3.16) * mm});
            skLineSegment(sketch, "E320", {"start": v(0.66, 3.16) * mm, "end": v(0.9, 3.2) * mm});
            skLineSegment(sketch, "E321", {"start": v(0.9, 3.2) * mm, "end": v(0.99, 3.2) * mm});
            skLineSegment(sketch, "E322", {"start": v(0.99, 3.2) * mm, "end": v(1, 3.2) * mm});
            skLineSegment(sketch, "E323", {"start": v(1, 3.2) * mm, "end": v(1.02, 3.2) * mm});
            skLineSegment(sketch, "E324", {"start": v(1.02, 3.2) * mm, "end": v(1.06, 3.17) * mm});
            skLineSegment(sketch, "E325", {"start": v(1.06, 3.17) * mm, "end": v(1.1, 3.13) * mm});
            skLineSegment(sketch, "E326", {"start": v(1.1, 3.13) * mm, "end": v(1.16, 3.09) * mm});
            skLineSegment(sketch, "E327", {"start": v(1.16, 3.09) * mm, "end": v(1.21, 3.03) * mm});
            skLineSegment(sketch, "E328", {"start": v(1.21, 3.03) * mm, "end": v(1.27, 2.97) * mm});
            skLineSegment(sketch, "E329", {"start": v(1.27, 2.97) * mm, "end": v(1.32, 2.89) * mm});
            skLineSegment(sketch, "E330", {"start": v(1.32, 2.89) * mm, "end": v(1.37, 2.8) * mm});
            skLineSegment(sketch, "E331", {"start": v(1.37, 2.8) * mm, "end": v(1.4, 2.7) * mm});
            skLineSegment(sketch, "E332", {"start": v(1.4, 2.7) * mm, "end": v(1.42, 2.6) * mm});
            skLineSegment(sketch, "E333", {"start": v(1.42, 2.6) * mm, "end": v(1.43, 2.48) * mm});
            skLineSegment(sketch, "E334", {"start": v(1.43, 2.48) * mm, "end": v(1.42, 2.35) * mm});
            skLineSegment(sketch, "E335", {"start": v(1.42, 2.35) * mm, "end": v(1.39, 2.2) * mm});
            skLineSegment(sketch, "E336", {"start": v(1.39, 2.2) * mm, "end": v(1.33, 2.05) * mm});
            skLineSegment(sketch, "E337", {"start": v(1.33, 2.05) * mm, "end": v(1.26, 1.93) * mm});
            skLineSegment(sketch, "E338", {"start": v(1.26, 1.93) * mm, "end": v(1.24, 1.89) * mm});
            skLineSegment(sketch, "E339", {"start": v(1.24, 1.89) * mm, "end": v(1.22, 1.89) * mm});
            skLineSegment(sketch, "E340", {"start": v(1.22, 1.89) * mm, "end": v(1.15, 1.88) * mm});
            skLineSegment(sketch, "E341", {"start": v(1.15, 1.88) * mm, "end": v(1.04, 1.87) * mm});
            skLineSegment(sketch, "E342", {"start": v(1.04, 1.87) * mm, "end": v(0.9, 1.84) * mm});
            skLineSegment(sketch, "E343", {"start": v(0.9, 1.84) * mm, "end": v(0.74, 1.8) * mm});
            skLineSegment(sketch, "E344", {"start": v(0.74, 1.8) * mm, "end": v(0.56, 1.74) * mm});
            skLineSegment(sketch, "E345", {"start": v(0.56, 1.74) * mm, "end": v(0.37, 1.65) * mm});
            skLineSegment(sketch, "E346", {"start": v(0.37, 1.65) * mm, "end": v(0.18, 1.55) * mm});
            skLineSegment(sketch, "E347", {"start": v(0.18, 1.55) * mm, "end": v(-0.02, 1.4) * mm});
            skLineSegment(sketch, "E348", {"start": v(-0.02, 1.4) * mm, "end": v(-0.2, 1.24) * mm});
            skLineSegment(sketch, "E349", {"start": v(-0.2, 1.24) * mm, "end": v(-0.37, 1.03) * mm});
            skLineSegment(sketch, "E350", {"start": v(-0.37, 1.03) * mm, "end": v(-0.52, 0.79) * mm});
            skLineSegment(sketch, "E351", {"start": v(-0.52, 0.79) * mm, "end": v(-0.65, 0.5) * mm});
            skLineSegment(sketch, "E352", {"start": v(-0.65, 0.5) * mm, "end": v(-0.74, 0.16) * mm});
            skLineSegment(sketch, "E353", {"start": v(-0.74, 0.16) * mm, "end": v(-0.78, -0.22) * mm});
            skLineSegment(sketch, "E354", {"start": v(-0.78, -0.22) * mm, "end": v(-0.79, -0.55) * mm});
            skLineSegment(sketch, "E355", {"start": v(-0.79, -0.55) * mm, "end": v(-0.78, -0.66) * mm});
            skLineSegment(sketch, "E356", {"start": v(0.82, 2.98) * mm, "end": v(0.84, 3) * mm});
            skLineSegment(sketch, "E357", {"start": v(0.84, 3) * mm, "end": v(0.88, 3.03) * mm});
            skLineSegment(sketch, "E358", {"start": v(0.88, 3.03) * mm, "end": v(0.96, 3.06) * mm});
            skLineSegment(sketch, "E359", {"start": v(0.96, 3.06) * mm, "end": v(1.03, 3.06) * mm});
            skLineSegment(sketch, "E360", {"start": v(1.03, 3.06) * mm, "end": v(1.09, 3.04) * mm});
            skLineSegment(sketch, "E361", {"start": v(1.09, 3.04) * mm, "end": v(1.1, 3.03) * mm});
            skLineSegment(sketch, "E362", {"start": v(1.1, 3.03) * mm, "end": v(1.12, 3.01) * mm});
            skLineSegment(sketch, "E363", {"start": v(1.12, 3.01) * mm, "end": v(1.16, 2.97) * mm});
            skLineSegment(sketch, "E364", {"start": v(1.16, 2.97) * mm, "end": v(1.19, 2.9) * mm});
            skLineSegment(sketch, "E365", {"start": v(1.19, 2.9) * mm, "end": v(1.18, 2.82) * mm});
            skLineSegment(sketch, "E366", {"start": v(1.18, 2.82) * mm, "end": v(1.16, 2.76) * mm});
            skLineSegment(sketch, "E367", {"start": v(1.16, 2.76) * mm, "end": v(1.15, 2.74) * mm});
            skLineSegment(sketch, "E368", {"start": v(1.15, 2.74) * mm, "end": v(1.14, 2.73) * mm});
            skLineSegment(sketch, "E369", {"start": v(1.14, 2.73) * mm, "end": v(1.1, 2.69) * mm});
            skLineSegment(sketch, "E370", {"start": v(1.1, 2.69) * mm, "end": v(1.02, 2.66) * mm});
            skLineSegment(sketch, "E371", {"start": v(1.02, 2.66) * mm, "end": v(0.94, 2.66) * mm});
            skLineSegment(sketch, "E372", {"start": v(0.94, 2.66) * mm, "end": v(0.89, 2.69) * mm});
            skLineSegment(sketch, "E373", {"start": v(0.89, 2.69) * mm, "end": v(0.87, 2.7) * mm});
            skLineSegment(sketch, "E374", {"start": v(0.87, 2.7) * mm, "end": v(0.86, 2.7) * mm});
            skLineSegment(sketch, "E375", {"start": v(0.86, 2.7) * mm, "end": v(0.82, 2.76) * mm});
            skLineSegment(sketch, "E376", {"start": v(0.82, 2.76) * mm, "end": v(0.79, 2.83) * mm});
            skLineSegment(sketch, "E377", {"start": v(0.79, 2.83) * mm, "end": v(0.8, 2.9) * mm});
            skLineSegment(sketch, "E378", {"start": v(0.8, 2.9) * mm, "end": v(0.81, 2.96) * mm});
            skLineSegment(sketch, "E379", {"start": v(0.81, 2.96) * mm, "end": v(0.82, 2.98) * mm});
            skLineSegment(sketch, "E380", {"start": v(-0.53, 2.5) * mm, "end": v(-0.52, 2.52) * mm});
            skLineSegment(sketch, "E381", {"start": v(-0.52, 2.52) * mm, "end": v(-0.47, 2.56) * mm});
            skLineSegment(sketch, "E382", {"start": v(-0.47, 2.56) * mm, "end": v(-0.4, 2.58) * mm});
            skLineSegment(sketch, "E383", {"start": v(-0.4, 2.58) * mm, "end": v(-0.32, 2.58) * mm});
            skLineSegment(sketch, "E384", {"start": v(-0.32, 2.58) * mm, "end": v(-0.27, 2.56) * mm});
            skLineSegment(sketch, "E385", {"start": v(-0.27, 2.56) * mm, "end": v(-0.25, 2.55) * mm});
            skLineSegment(sketch, "E386", {"start": v(-0.25, 2.55) * mm, "end": v(-0.24, 2.54) * mm});
            skLineSegment(sketch, "E387", {"start": v(-0.24, 2.54) * mm, "end": v(-0.2, 2.5) * mm});
            skLineSegment(sketch, "E388", {"start": v(-0.2, 2.5) * mm, "end": v(-0.17, 2.42) * mm});
            skLineSegment(sketch, "E389", {"start": v(-0.17, 2.42) * mm, "end": v(-0.17, 2.34) * mm});
            skLineSegment(sketch, "E390", {"start": v(-0.17, 2.34) * mm, "end": v(-0.2, 2.28) * mm});
            skLineSegment(sketch, "E391", {"start": v(-0.2, 2.28) * mm, "end": v(-0.2, 2.27) * mm});
            skLineSegment(sketch, "E392", {"start": v(-0.2, 2.27) * mm, "end": v(-0.22, 2.25) * mm});
            skLineSegment(sketch, "E393", {"start": v(-0.22, 2.25) * mm, "end": v(-0.26, 2.21) * mm});
            skLineSegment(sketch, "E394", {"start": v(-0.26, 2.21) * mm, "end": v(-0.34, 2.19) * mm});
            skLineSegment(sketch, "E395", {"start": v(-0.34, 2.19) * mm, "end": v(-0.41, 2.19) * mm});
            skLineSegment(sketch, "E396", {"start": v(-0.41, 2.19) * mm, "end": v(-0.47, 2.2) * mm});
            skLineSegment(sketch, "E397", {"start": v(-0.47, 2.2) * mm, "end": v(-0.49, 2.22) * mm});
            skLineSegment(sketch, "E398", {"start": v(-0.49, 2.22) * mm, "end": v(-0.5, 2.23) * mm});
            skLineSegment(sketch, "E399", {"start": v(-0.5, 2.23) * mm, "end": v(-0.54, 2.28) * mm});
            skLineSegment(sketch, "E400", {"start": v(-0.54, 2.28) * mm, "end": v(-0.57, 2.35) * mm});
            skLineSegment(sketch, "E401", {"start": v(-0.57, 2.35) * mm, "end": v(-0.57, 2.43) * mm});
            skLineSegment(sketch, "E402", {"start": v(-0.57, 2.43) * mm, "end": v(-0.54, 2.49) * mm});
            skLineSegment(sketch, "E403", {"start": v(-0.54, 2.49) * mm, "end": v(-0.53, 2.5) * mm});
            skLineSegment(sketch, "E404", {"start": v(0.35, -1.02) * mm, "end": v(0.35, -1.04) * mm});
            skLineSegment(sketch, "E405", {"start": v(0.35, -1.04) * mm, "end": v(0.37, -1.09) * mm});
            skLineSegment(sketch, "E406", {"start": v(0.37, -1.09) * mm, "end": v(0.39, -1.16) * mm});
            skLineSegment(sketch, "E407", {"start": v(0.39, -1.16) * mm, "end": v(0.4, -1.25) * mm});
            skLineSegment(sketch, "E408", {"start": v(0.4, -1.25) * mm, "end": v(0.4, -1.36) * mm});
            skLineSegment(sketch, "E409", {"start": v(0.4, -1.36) * mm, "end": v(0.37, -1.46) * mm});
            skLineSegment(sketch, "E410", {"start": v(0.37, -1.46) * mm, "end": v(0.33, -1.57) * mm});
            skLineSegment(sketch, "E411", {"start": v(0.33, -1.57) * mm, "end": v(0.27, -1.64) * mm});
            skLineSegment(sketch, "E412", {"start": v(0.27, -1.64) * mm, "end": v(0.25, -1.66) * mm});
            skLineSegment(sketch, "E413", {"start": v(0.25, -1.66) * mm, "end": v(0.24, -1.66) * mm});
            skLineSegment(sketch, "E414", {"start": v(0.24, -1.66) * mm, "end": v(0.2, -1.66) * mm});
            skLineSegment(sketch, "E415", {"start": v(0.2, -1.66) * mm, "end": v(0.15, -1.66) * mm});
            skLineSegment(sketch, "E416", {"start": v(0.15, -1.66) * mm, "end": v(0.08, -1.66) * mm});
            skLineSegment(sketch, "E417", {"start": v(0.08, -1.66) * mm, "end": v(0, -1.65) * mm});
            skLineSegment(sketch, "E418", {"start": v(0, -1.65) * mm, "end": v(-0.1, -1.64) * mm});
            skLineSegment(sketch, "E419", {"start": v(-0.1, -1.64) * mm, "end": v(-0.21, -1.63) * mm});
            skLineSegment(sketch, "E420", {"start": v(-0.21, -1.63) * mm, "end": v(-0.34, -1.62) * mm});
            skLineSegment(sketch, "E421", {"start": v(-0.34, -1.62) * mm, "end": v(-0.47, -1.6) * mm});
            skLineSegment(sketch, "E422", {"start": v(-0.47, -1.6) * mm, "end": v(-0.61, -1.57) * mm});
            skLineSegment(sketch, "E423", {"start": v(-0.61, -1.57) * mm, "end": v(-0.76, -1.53) * mm});
            skLineSegment(sketch, "E424", {"start": v(-0.76, -1.53) * mm, "end": v(-0.91, -1.5) * mm});
            skLineSegment(sketch, "E425", {"start": v(-0.91, -1.5) * mm, "end": v(-1.07, -1.45) * mm});
            skLineSegment(sketch, "E426", {"start": v(-1.07, -1.45) * mm, "end": v(-1.23, -1.39) * mm});
            skLineSegment(sketch, "E427", {"start": v(-1.23, -1.39) * mm, "end": v(-1.4, -1.32) * mm});
            skLineSegment(sketch, "E428", {"start": v(-1.4, -1.32) * mm, "end": v(-1.56, -1.25) * mm});
            skLineSegment(sketch, "E429", {"start": v(-1.56, -1.25) * mm, "end": v(-1.71, -1.16) * mm});
            skLineSegment(sketch, "E430", {"start": v(-1.71, -1.16) * mm, "end": v(-1.87, -1.06) * mm});
            skLineSegment(sketch, "E431", {"start": v(-1.87, -1.06) * mm, "end": v(-2.02, -0.95) * mm});
            skLineSegment(sketch, "E432", {"start": v(-2.02, -0.95) * mm, "end": v(-2.16, -0.83) * mm});
            skLineSegment(sketch, "E433", {"start": v(-2.16, -0.83) * mm, "end": v(-2.3, -0.7) * mm});
            skLineSegment(sketch, "E434", {"start": v(-2.3, -0.7) * mm, "end": v(-2.41, -0.54) * mm});
            skLineSegment(sketch, "E435", {"start": v(-2.41, -0.54) * mm, "end": v(-2.53, -0.38) * mm});
            skLineSegment(sketch, "E436", {"start": v(-2.53, -0.38) * mm, "end": v(-2.63, -0.2) * mm});
            skLineSegment(sketch, "E437", {"start": v(-2.63, -0.2) * mm, "end": v(-2.7, 0) * mm});
            skLineSegment(sketch, "E438", {"start": v(-2.7, 0) * mm, "end": v(-2.78, 0.21) * mm});
            skLineSegment(sketch, "E439", {"start": v(-2.78, 0.21) * mm, "end": v(-2.83, 0.45) * mm});
            skLineSegment(sketch, "E440", {"start": v(-2.83, 0.45) * mm, "end": v(-2.86, 0.7) * mm});
            skLineSegment(sketch, "E441", {"start": v(-2.86, 0.7) * mm, "end": v(-2.87, 0.96) * mm});
            skLineSegment(sketch, "E442", {"start": v(-2.87, 0.96) * mm, "end": v(-2.86, 1.25) * mm});
            skLineSegment(sketch, "E443", {"start": v(-2.86, 1.25) * mm, "end": v(-2.82, 1.56) * mm});
            skLineSegment(sketch, "E444", {"start": v(-2.82, 1.56) * mm, "end": v(-2.78, 1.8) * mm});
            skLineSegment(sketch, "E445", {"start": v(-2.78, 1.8) * mm, "end": v(-2.76, 1.9) * mm});
            skLineSegment(sketch, "E446", {"start": v(-2.76, 1.9) * mm, "end": v(-2.75, 1.9) * mm});
            skLineSegment(sketch, "E447", {"start": v(-2.75, 1.9) * mm, "end": v(-2.73, 1.92) * mm});
            skLineSegment(sketch, "E448", {"start": v(-2.73, 1.92) * mm, "end": v(-2.7, 1.94) * mm});
            skLineSegment(sketch, "E449", {"start": v(-2.7, 1.94) * mm, "end": v(-2.65, 1.98) * mm});
            skLineSegment(sketch, "E450", {"start": v(-2.65, 1.98) * mm, "end": v(-2.59, 2.01) * mm});
            skLineSegment(sketch, "E451", {"start": v(-2.59, 2.01) * mm, "end": v(-2.52, 2.05) * mm});
            skLineSegment(sketch, "E452", {"start": v(-2.52, 2.05) * mm, "end": v(-2.44, 2.08) * mm});
            skLineSegment(sketch, "E453", {"start": v(-2.44, 2.08) * mm, "end": v(-2.35, 2.1) * mm});
            skLineSegment(sketch, "E454", {"start": v(-2.35, 2.1) * mm, "end": v(-2.25, 2.12) * mm});
            skLineSegment(sketch, "E455", {"start": v(-2.25, 2.12) * mm, "end": v(-2.15, 2.12) * mm});
            skLineSegment(sketch, "E456", {"start": v(-2.15, 2.12) * mm, "end": v(-2.04, 2.1) * mm});
            skLineSegment(sketch, "E457", {"start": v(-2.04, 2.1) * mm, "end": v(-1.92, 2.08) * mm});
            skLineSegment(sketch, "E458", {"start": v(-1.92, 2.08) * mm, "end": v(-1.8, 2.02) * mm});
            skLineSegment(sketch, "E459", {"start": v(-1.8, 2.02) * mm, "end": v(-1.68, 1.95) * mm});
            skLineSegment(sketch, "E460", {"start": v(-1.68, 1.95) * mm, "end": v(-1.55, 1.84) * mm});
            skLineSegment(sketch, "E461", {"start": v(-1.55, 1.84) * mm, "end": v(-1.46, 1.74) * mm});
            skLineSegment(sketch, "E462", {"start": v(-1.46, 1.74) * mm, "end": v(-1.43, 1.7) * mm});
            skLineSegment(sketch, "E463", {"start": v(-1.43, 1.7) * mm, "end": v(-1.43, 1.7) * mm});
            skLineSegment(sketch, "E464", {"start": v(-1.43, 1.7) * mm, "end": v(-1.43, 1.69) * mm});
            skLineSegment(sketch, "E465", {"start": v(-1.43, 1.69) * mm, "end": v(-1.44, 1.66) * mm});
            skLineSegment(sketch, "E466", {"start": v(-1.44, 1.66) * mm, "end": v(-1.45, 1.62) * mm});
            skLineSegment(sketch, "E467", {"start": v(-1.45, 1.62) * mm, "end": v(-1.46, 1.57) * mm});
            skLineSegment(sketch, "E468", {"start": v(-1.46, 1.57) * mm, "end": v(-1.47, 1.51) * mm});
            skLineSegment(sketch, "E469", {"start": v(-1.47, 1.51) * mm, "end": v(-1.48, 1.45) * mm});
            skLineSegment(sketch, "E470", {"start": v(-1.48, 1.45) * mm, "end": v(-1.49, 1.38) * mm});
            skLineSegment(sketch, "E471", {"start": v(-1.49, 1.38) * mm, "end": v(-1.5, 1.3) * mm});
            skLineSegment(sketch, "E472", {"start": v(-1.5, 1.3) * mm, "end": v(-1.5, 1.2) * mm});
            skLineSegment(sketch, "E473", {"start": v(-1.5, 1.2) * mm, "end": v(-1.5, 1.12) * mm});
            skLineSegment(sketch, "E474", {"start": v(-1.5, 1.12) * mm, "end": v(-1.5, 1.02) * mm});
            skLineSegment(sketch, "E475", {"start": v(-1.5, 1.02) * mm, "end": v(-1.5, 0.92) * mm});
            skLineSegment(sketch, "E476", {"start": v(-1.5, 0.92) * mm, "end": v(-1.48, 0.81) * mm});
            skLineSegment(sketch, "E477", {"start": v(-1.48, 0.81) * mm, "end": v(-1.46, 0.7) * mm});
            skLineSegment(sketch, "E478", {"start": v(-1.46, 0.7) * mm, "end": v(-1.44, 0.6) * mm});
            skLineSegment(sketch, "E479", {"start": v(-1.44, 0.6) * mm, "end": v(-1.4, 0.48) * mm});
            skLineSegment(sketch, "E480", {"start": v(-1.4, 0.48) * mm, "end": v(-1.37, 0.36) * mm});
            skLineSegment(sketch, "E481", {"start": v(-1.37, 0.36) * mm, "end": v(-1.32, 0.25) * mm});
            skLineSegment(sketch, "E482", {"start": v(-1.32, 0.25) * mm, "end": v(-1.27, 0.13) * mm});
            skLineSegment(sketch, "E483", {"start": v(-1.27, 0.13) * mm, "end": v(-1.2, 0.02) * mm});
            skLineSegment(sketch, "E484", {"start": v(-1.2, 0.02) * mm, "end": v(-1.13, -0.1) * mm});
            skLineSegment(sketch, "E485", {"start": v(-1.13, -0.1) * mm, "end": v(-1.04, -0.2) * mm});
            skLineSegment(sketch, "E486", {"start": v(-1.04, -0.2) * mm, "end": v(-0.94, -0.31) * mm});
            skLineSegment(sketch, "E487", {"start": v(-0.94, -0.31) * mm, "end": v(-0.83, -0.42) * mm});
            skLineSegment(sketch, "E488", {"start": v(-0.83, -0.42) * mm, "end": v(-0.7, -0.52) * mm});
            skLineSegment(sketch, "E489", {"start": v(-0.7, -0.52) * mm, "end": v(-0.57, -0.62) * mm});
            skLineSegment(sketch, "E490", {"start": v(-0.57, -0.62) * mm, "end": v(-0.42, -0.71) * mm});
            skLineSegment(sketch, "E491", {"start": v(-0.42, -0.71) * mm, "end": v(-0.25, -0.8) * mm});
            skLineSegment(sketch, "E492", {"start": v(-0.25, -0.8) * mm, "end": v(-0.07, -0.88) * mm});
            skLineSegment(sketch, "E493", {"start": v(-0.07, -0.88) * mm, "end": v(0.13, -0.95) * mm});
            skLineSegment(sketch, "E494", {"start": v(0.13, -0.95) * mm, "end": v(0.3, -1) * mm});
            skLineSegment(sketch, "E495", {"start": v(0.3, -1) * mm, "end": v(0.35, -1.02) * mm});
            skLineSegment(sketch, "E496", {"start": v(-2.6, 1.66) * mm, "end": v(-2.6, 1.68) * mm});
            skLineSegment(sketch, "E497", {"start": v(-2.6, 1.68) * mm, "end": v(-2.63, 1.73) * mm});
            skLineSegment(sketch, "E498", {"start": v(-2.63, 1.73) * mm, "end": v(-2.63, 1.81) * mm});
            skLineSegment(sketch, "E499", {"start": v(-2.63, 1.81) * mm, "end": v(-2.6, 1.88) * mm});
            skLineSegment(sketch, "E500", {"start": v(-2.6, 1.88) * mm, "end": v(-2.56, 1.93) * mm});
            skLineSegment(sketch, "E501", {"start": v(-2.56, 1.93) * mm, "end": v(-2.55, 1.94) * mm});
            skLineSegment(sketch, "E502", {"start": v(-2.55, 1.94) * mm, "end": v(-2.53, 1.95) * mm});
            skLineSegment(sketch, "E503", {"start": v(-2.53, 1.95) * mm, "end": v(-2.47, 1.97) * mm});
            skLineSegment(sketch, "E504", {"start": v(-2.47, 1.97) * mm, "end": v(-2.4, 1.98) * mm});
            skLineSegment(sketch, "E505", {"start": v(-2.4, 1.98) * mm, "end": v(-2.32, 1.95) * mm});
            skLineSegment(sketch, "E506", {"start": v(-2.32, 1.95) * mm, "end": v(-2.28, 1.91) * mm});
            skLineSegment(sketch, "E507", {"start": v(-2.28, 1.91) * mm, "end": v(-2.27, 1.9) * mm});
            skLineSegment(sketch, "E508", {"start": v(-2.27, 1.9) * mm, "end": v(-2.25, 1.88) * mm});
            skLineSegment(sketch, "E509", {"start": v(-2.25, 1.88) * mm, "end": v(-2.23, 1.82) * mm});
            skLineSegment(sketch, "E510", {"start": v(-2.23, 1.82) * mm, "end": v(-2.23, 1.75) * mm});
            skLineSegment(sketch, "E511", {"start": v(-2.23, 1.75) * mm, "end": v(-2.26, 1.67) * mm});
            skLineSegment(sketch, "E512", {"start": v(-2.26, 1.67) * mm, "end": v(-2.3, 1.63) * mm});
            skLineSegment(sketch, "E513", {"start": v(-2.3, 1.63) * mm, "end": v(-2.31, 1.62) * mm});
            skLineSegment(sketch, "E514", {"start": v(-2.31, 1.62) * mm, "end": v(-2.33, 1.6) * mm});
            skLineSegment(sketch, "E515", {"start": v(-2.33, 1.6) * mm, "end": v(-2.38, 1.58) * mm});
            skLineSegment(sketch, "E516", {"start": v(-2.38, 1.58) * mm, "end": v(-2.46, 1.58) * mm});
            skLineSegment(sketch, "E517", {"start": v(-2.46, 1.58) * mm, "end": v(-2.53, 1.6) * mm});
            skLineSegment(sketch, "E518", {"start": v(-2.53, 1.6) * mm, "end": v(-2.58, 1.64) * mm});
            skLineSegment(sketch, "E519", {"start": v(-2.58, 1.64) * mm, "end": v(-2.6, 1.66) * mm});
            skLineSegment(sketch, "E520", {"start": v(-2.57, 0.22) * mm, "end": v(-2.58, 0.24) * mm});
            skLineSegment(sketch, "E521", {"start": v(-2.58, 0.24) * mm, "end": v(-2.6, 0.3) * mm});
            skLineSegment(sketch, "E522", {"start": v(-2.6, 0.3) * mm, "end": v(-2.6, 0.37) * mm});
            skLineSegment(sketch, "E523", {"start": v(-2.6, 0.37) * mm, "end": v(-2.58, 0.44) * mm});
            skLineSegment(sketch, "E524", {"start": v(-2.58, 0.44) * mm, "end": v(-2.54, 0.5) * mm});
            skLineSegment(sketch, "E525", {"start": v(-2.54, 0.5) * mm, "end": v(-2.53, 0.5) * mm});
            skLineSegment(sketch, "E526", {"start": v(-2.53, 0.5) * mm, "end": v(-2.51, 0.52) * mm});
            skLineSegment(sketch, "E527", {"start": v(-2.51, 0.52) * mm, "end": v(-2.45, 0.54) * mm});
            skLineSegment(sketch, "E528", {"start": v(-2.45, 0.54) * mm, "end": v(-2.38, 0.54) * mm});
            skLineSegment(sketch, "E529", {"start": v(-2.38, 0.54) * mm, "end": v(-2.3, 0.51) * mm});
            skLineSegment(sketch, "E530", {"start": v(-2.3, 0.51) * mm, "end": v(-2.26, 0.47) * mm});
            skLineSegment(sketch, "E531", {"start": v(-2.26, 0.47) * mm, "end": v(-2.25, 0.46) * mm});
            skLineSegment(sketch, "E532", {"start": v(-2.25, 0.46) * mm, "end": v(-2.23, 0.44) * mm});
            skLineSegment(sketch, "E533", {"start": v(-2.23, 0.44) * mm, "end": v(-2.21, 0.39) * mm});
            skLineSegment(sketch, "E534", {"start": v(-2.21, 0.39) * mm, "end": v(-2.2, 0.3) * mm});
            skLineSegment(sketch, "E535", {"start": v(-2.2, 0.3) * mm, "end": v(-2.24, 0.24) * mm});
            skLineSegment(sketch, "E536", {"start": v(-2.24, 0.24) * mm, "end": v(-2.27, 0.19) * mm});
            skLineSegment(sketch, "E537", {"start": v(-2.27, 0.19) * mm, "end": v(-2.3, 0.18) * mm});
            skLineSegment(sketch, "E538", {"start": v(-2.3, 0.18) * mm, "end": v(-2.3, 0.17) * mm});
            skLineSegment(sketch, "E539", {"start": v(-2.3, 0.17) * mm, "end": v(-2.36, 0.14) * mm});
            skLineSegment(sketch, "E540", {"start": v(-2.36, 0.14) * mm, "end": v(-2.44, 0.14) * mm});
            skLineSegment(sketch, "E541", {"start": v(-2.44, 0.14) * mm, "end": v(-2.51, 0.17) * mm});
            skLineSegment(sketch, "E542", {"start": v(-2.51, 0.17) * mm, "end": v(-2.56, 0.2) * mm});
            skLineSegment(sketch, "E543", {"start": v(-2.56, 0.2) * mm, "end": v(-2.57, 0.22) * mm});
            skLineSegment(sketch, "E544", {"start": v(1.04, 0.01) * mm, "end": v(1.06, 0.01) * mm});
            skLineSegment(sketch, "E545", {"start": v(1.06, 0.01) * mm, "end": v(1.1, 0.01) * mm});
            skLineSegment(sketch, "E546", {"start": v(1.1, 0.01) * mm, "end": v(1.18, 0) * mm});
            skLineSegment(sketch, "E547", {"start": v(1.18, 0) * mm, "end": v(1.28, -0.01) * mm});
            skLineSegment(sketch, "E548", {"start": v(1.28, -0.01) * mm, "end": v(1.37, -0.05) * mm});
            skLineSegment(sketch, "E549", {"start": v(1.37, -0.05) * mm, "end": v(1.47, -0.1) * mm});
            skLineSegment(sketch, "E550", {"start": v(1.47, -0.1) * mm, "end": v(1.55, -0.18) * mm});
            skLineSegment(sketch, "E551", {"start": v(1.55, -0.18) * mm, "end": v(1.6, -0.25) * mm});
            skLineSegment(sketch, "E552", {"start": v(1.6, -0.25) * mm, "end": v(1.61, -0.28) * mm});
            skLineSegment(sketch, "E553", {"start": v(1.61, -0.28) * mm, "end": v(1.61, -0.3) * mm});
            skLineSegment(sketch, "E554", {"start": v(1.61, -0.3) * mm, "end": v(1.6, -0.32) * mm});
            skLineSegment(sketch, "E555", {"start": v(1.6, -0.32) * mm, "end": v(1.58, -0.37) * mm});
            skLineSegment(sketch, "E556", {"start": v(1.58, -0.37) * mm, "end": v(1.56, -0.44) * mm});
            skLineSegment(sketch, "E557", {"start": v(1.56, -0.44) * mm, "end": v(1.53, -0.51) * mm});
            skLineSegment(sketch, "E558", {"start": v(1.53, -0.51) * mm, "end": v(1.5, -0.6) * mm});
            skLineSegment(sketch, "E559", {"start": v(1.5, -0.6) * mm, "end": v(1.45, -0.7) * mm});
            skLineSegment(sketch, "E560", {"start": v(1.45, -0.7) * mm, "end": v(1.4, -0.82) * mm});
            skLineSegment(sketch, "E561", {"start": v(1.4, -0.82) * mm, "end": v(1.33, -0.94) * mm});
            skLineSegment(sketch, "E562", {"start": v(1.33, -0.94) * mm, "end": v(1.26, -1.07) * mm});
            skLineSegment(sketch, "E563", {"start": v(1.26, -1.07) * mm, "end": v(1.18, -1.2) * mm});
            skLineSegment(sketch, "E564", {"start": v(1.18, -1.2) * mm, "end": v(1.1, -1.34) * mm});
            skLineSegment(sketch, "E565", {"start": v(1.1, -1.34) * mm, "end": v(1, -1.47) * mm});
            skLineSegment(sketch, "E566", {"start": v(1, -1.47) * mm, "end": v(0.9, -1.6) * mm});
            skLineSegment(sketch, "E567", {"start": v(0.9, -1.6) * mm, "end": v(0.79, -1.74) * mm});
            skLineSegment(sketch, "E568", {"start": v(0.79, -1.74) * mm, "end": v(0.66, -1.87) * mm});
            skLineSegment(sketch, "E569", {"start": v(0.66, -1.87) * mm, "end": v(0.53, -2) * mm});
            skLineSegment(sketch, "E570", {"start": v(0.53, -2) * mm, "end": v(0.4, -2.1) * mm});
            skLineSegment(sketch, "E571", {"start": v(0.4, -2.1) * mm, "end": v(0.24, -2.22) * mm});
            skLineSegment(sketch, "E572", {"start": v(0.24, -2.22) * mm, "end": v(0.08, -2.31) * mm});
            skLineSegment(sketch, "E573", {"start": v(0.08, -2.31) * mm, "end": v(-0.09, -2.4) * mm});
            skLineSegment(sketch, "E574", {"start": v(-0.09, -2.4) * mm, "end": v(-0.27, -2.47) * mm});
            skLineSegment(sketch, "E575", {"start": v(-0.27, -2.47) * mm, "end": v(-0.46, -2.52) * mm});
            skLineSegment(sketch, "E576", {"start": v(-0.46, -2.52) * mm, "end": v(-0.66, -2.56) * mm});
            skLineSegment(sketch, "E577", {"start": v(-0.66, -2.56) * mm, "end": v(-0.88, -2.58) * mm});
            skLineSegment(sketch, "E578", {"start": v(-0.88, -2.58) * mm, "end": v(-1.1, -2.58) * mm});
            skLineSegment(sketch, "E579", {"start": v(-1.1, -2.58) * mm, "end": v(-1.34, -2.56) * mm});
            skLineSegment(sketch, "E580", {"start": v(-1.34, -2.56) * mm, "end": v(-1.59, -2.5) * mm});
            skLineSegment(sketch, "E581", {"start": v(-1.59, -2.5) * mm, "end": v(-1.84, -2.43) * mm});
            skLineSegment(sketch, "E582", {"start": v(-1.84, -2.43) * mm, "end": v(-2.11, -2.33) * mm});
            skLineSegment(sketch, "E583", {"start": v(-2.11, -2.33) * mm, "end": v(-2.4, -2.2) * mm});
            skLineSegment(sketch, "E584", {"start": v(-2.4, -2.2) * mm, "end": v(-2.62, -2.09) * mm});
            skLineSegment(sketch, "E585", {"start": v(-2.62, -2.09) * mm, "end": v(-2.7, -2.04) * mm});
            skLineSegment(sketch, "E586", {"start": v(-2.7, -2.04) * mm, "end": v(-2.7, -2.03) * mm});
            skLineSegment(sketch, "E587", {"start": v(-2.7, -2.03) * mm, "end": v(-2.7, -2) * mm});
            skLineSegment(sketch, "E588", {"start": v(-2.7, -2) * mm, "end": v(-2.72, -1.97) * mm});
            skLineSegment(sketch, "E589", {"start": v(-2.72, -1.97) * mm, "end": v(-2.74, -1.91) * mm});
            skLineSegment(sketch, "E590", {"start": v(-2.74, -1.91) * mm, "end": v(-2.75, -1.84) * mm});
            skLineSegment(sketch, "E591", {"start": v(-2.75, -1.84) * mm, "end": v(-2.76, -1.77) * mm});
            skLineSegment(sketch, "E592", {"start": v(-2.76, -1.77) * mm, "end": v(-2.77, -1.68) * mm});
            skLineSegment(sketch, "E593", {"start": v(-2.77, -1.68) * mm, "end": v(-2.77, -1.59) * mm});
            skLineSegment(sketch, "E594", {"start": v(-2.77, -1.59) * mm, "end": v(-2.75, -1.5) * mm});
            skLineSegment(sketch, "E595", {"start": v(-2.75, -1.5) * mm, "end": v(-2.72, -1.4) * mm});
            skLineSegment(sketch, "E596", {"start": v(-2.72, -1.4) * mm, "end": v(-2.67, -1.3) * mm});
            skLineSegment(sketch, "E597", {"start": v(-2.67, -1.3) * mm, "end": v(-2.6, -1.2) * mm});
            skLineSegment(sketch, "E598", {"start": v(-2.6, -1.2) * mm, "end": v(-2.52, -1.1) * mm});
            skLineSegment(sketch, "E599", {"start": v(-2.52, -1.1) * mm, "end": v(-2.41, -1) * mm});
            skLineSegment(sketch, "E600", {"start": v(-2.41, -1) * mm, "end": v(-2.27, -0.91) * mm});
            skLineSegment(sketch, "E601", {"start": v(-2.27, -0.91) * mm, "end": v(-2.15, -0.85) * mm});
            skLineSegment(sketch, "E602", {"start": v(-2.15, -0.85) * mm, "end": v(-2.1, -0.83) * mm});
            skLineSegment(sketch, "E603", {"start": v(-2.1, -0.83) * mm, "end": v(-2.1, -0.84) * mm});
            skLineSegment(sketch, "E604", {"start": v(-2.1, -0.84) * mm, "end": v(-2.09, -0.84) * mm});
            skLineSegment(sketch, "E605", {"start": v(-2.09, -0.84) * mm, "end": v(-2.06, -0.86) * mm});
            skLineSegment(sketch, "E606", {"start": v(-2.06, -0.86) * mm, "end": v(-2.03, -0.88) * mm});
            skLineSegment(sketch, "E607", {"start": v(-2.03, -0.88) * mm, "end": v(-1.98, -0.9) * mm});
            skLineSegment(sketch, "E608", {"start": v(-1.98, -0.9) * mm, "end": v(-1.93, -0.93) * mm});
            skLineSegment(sketch, "E609", {"start": v(-1.93, -0.93) * mm, "end": v(-1.87, -0.96) * mm});
            skLineSegment(sketch, "E610", {"start": v(-1.87, -0.96) * mm, "end": v(-1.8, -1) * mm});
            skLineSegment(sketch, "E611", {"start": v(-1.8, -1) * mm, "end": v(-1.73, -1.02) * mm});
            skLineSegment(sketch, "E612", {"start": v(-1.73, -1.02) * mm, "end": v(-1.65, -1.05) * mm});
            skLineSegment(sketch, "E613", {"start": v(-1.65, -1.05) * mm, "end": v(-1.57, -1.08) * mm});
            skLineSegment(sketch, "E614", {"start": v(-1.57, -1.08) * mm, "end": v(-1.47, -1.11) * mm});
            skLineSegment(sketch, "E615", {"start": v(-1.47, -1.11) * mm, "end": v(-1.37, -1.14) * mm});
            skLineSegment(sketch, "E616", {"start": v(-1.37, -1.14) * mm, "end": v(-1.27, -1.16) * mm});
            skLineSegment(sketch, "E617", {"start": v(-1.27, -1.16) * mm, "end": v(-1.16, -1.18) * mm});
            skLineSegment(sketch, "E618", {"start": v(-1.16, -1.18) * mm, "end": v(-1.05, -1.19) * mm});
            skLineSegment(sketch, "E619", {"start": v(-1.05, -1.19) * mm, "end": v(-0.93, -1.2) * mm});
            skLineSegment(sketch, "E620", {"start": v(-0.93, -1.2) * mm, "end": v(-0.8, -1.2) * mm});
            skLineSegment(sketch, "E621", {"start": v(-0.8, -1.2) * mm, "end": v(-0.69, -1.19) * mm});
            skLineSegment(sketch, "E622", {"start": v(-0.69, -1.19) * mm, "end": v(-0.56, -1.17) * mm});
            skLineSegment(sketch, "E623", {"start": v(-0.56, -1.17) * mm, "end": v(-0.43, -1.14) * mm});
            skLineSegment(sketch, "E624", {"start": v(-0.43, -1.14) * mm, "end": v(-0.3, -1.1) * mm});
            skLineSegment(sketch, "E625", {"start": v(-0.3, -1.1) * mm, "end": v(-0.17, -1.06) * mm});
            skLineSegment(sketch, "E626", {"start": v(-0.17, -1.06) * mm, "end": v(-0.03, -1) * mm});
            skLineSegment(sketch, "E627", {"start": v(-0.03, -1) * mm, "end": v(0.1, -0.92) * mm});
            skLineSegment(sketch, "E628", {"start": v(0.1, -0.92) * mm, "end": v(0.24, -0.84) * mm});
            skLineSegment(sketch, "E629", {"start": v(0.24, -0.84) * mm, "end": v(0.37, -0.74) * mm});
            skLineSegment(sketch, "E630", {"start": v(0.37, -0.74) * mm, "end": v(0.5, -0.62) * mm});
            skLineSegment(sketch, "E631", {"start": v(0.5, -0.62) * mm, "end": v(0.64, -0.49) * mm});
            skLineSegment(sketch, "E632", {"start": v(0.64, -0.49) * mm, "end": v(0.78, -0.34) * mm});
            skLineSegment(sketch, "E633", {"start": v(0.78, -0.34) * mm, "end": v(0.9, -0.17) * mm});
            skLineSegment(sketch, "E634", {"start": v(0.9, -0.17) * mm, "end": v(1, -0.04) * mm});
            skLineSegment(sketch, "E635", {"start": v(1, -0.04) * mm, "end": v(1.04, 0.01) * mm});
            skLineSegment(sketch, "E636", {"start": v(-2.42, -1.96) * mm, "end": v(-2.44, -1.96) * mm});
            skLineSegment(sketch, "E637", {"start": v(-2.44, -1.96) * mm, "end": v(-2.5, -1.96) * mm});
            skLineSegment(sketch, "E638", {"start": v(-2.5, -1.96) * mm, "end": v(-2.57, -1.94) * mm});
            skLineSegment(sketch, "E639", {"start": v(-2.57, -1.94) * mm, "end": v(-2.63, -1.9) * mm});
            skLineSegment(sketch, "E640", {"start": v(-2.63, -1.9) * mm, "end": v(-2.67, -1.84) * mm});
            skLineSegment(sketch, "E641", {"start": v(-2.67, -1.84) * mm, "end": v(-2.67, -1.83) * mm});
            skLineSegment(sketch, "E642", {"start": v(-2.67, -1.83) * mm, "end": v(-2.68, -1.8) * mm});
            skLineSegment(sketch, "E643", {"start": v(-2.68, -1.8) * mm, "end": v(-2.68, -1.75) * mm});
            skLineSegment(sketch, "E644", {"start": v(-2.68, -1.75) * mm, "end": v(-2.66, -1.67) * mm});
            skLineSegment(sketch, "E645", {"start": v(-2.66, -1.67) * mm, "end": v(-2.61, -1.61) * mm});
            skLineSegment(sketch, "E646", {"start": v(-2.61, -1.61) * mm, "end": v(-2.56, -1.58) * mm});
            skLineSegment(sketch, "E647", {"start": v(-2.56, -1.58) * mm, "end": v(-2.54, -1.57) * mm});
            skLineSegment(sketch, "E648", {"start": v(-2.54, -1.57) * mm, "end": v(-2.53, -1.57) * mm});
            skLineSegment(sketch, "E649", {"start": v(-2.53, -1.57) * mm, "end": v(-2.46, -1.56) * mm});
            skLineSegment(sketch, "E650", {"start": v(-2.46, -1.56) * mm, "end": v(-2.4, -1.58) * mm});
            skLineSegment(sketch, "E651", {"start": v(-2.4, -1.58) * mm, "end": v(-2.33, -1.63) * mm});
            skLineSegment(sketch, "E652", {"start": v(-2.33, -1.63) * mm, "end": v(-2.3, -1.68) * mm});
            skLineSegment(sketch, "E653", {"start": v(-2.3, -1.68) * mm, "end": v(-2.3, -1.7) * mm});
            skLineSegment(sketch, "E654", {"start": v(-2.3, -1.7) * mm, "end": v(-2.28, -1.72) * mm});
            skLineSegment(sketch, "E655", {"start": v(-2.28, -1.72) * mm, "end": v(-2.28, -1.78) * mm});
            skLineSegment(sketch, "E656", {"start": v(-2.28, -1.78) * mm, "end": v(-2.3, -1.86) * mm});
            skLineSegment(sketch, "E657", {"start": v(-2.3, -1.86) * mm, "end": v(-2.35, -1.92) * mm});
            skLineSegment(sketch, "E658", {"start": v(-2.35, -1.92) * mm, "end": v(-2.4, -1.95) * mm});
            skLineSegment(sketch, "E659", {"start": v(-2.4, -1.95) * mm, "end": v(-2.42, -1.96) * mm});
            skLineSegment(sketch, "E660", {"start": v(-1.05, -2.38) * mm, "end": v(-1.06, -2.39) * mm});
            skLineSegment(sketch, "E661", {"start": v(-1.06, -2.39) * mm, "end": v(-1.13, -2.39) * mm});
            skLineSegment(sketch, "E662", {"start": v(-1.13, -2.39) * mm, "end": v(-1.2, -2.37) * mm});
            skLineSegment(sketch, "E663", {"start": v(-1.2, -2.37) * mm, "end": v(-1.26, -2.32) * mm});
            skLineSegment(sketch, "E664", {"start": v(-1.26, -2.32) * mm, "end": v(-1.3, -2.27) * mm});
            skLineSegment(sketch, "E665", {"start": v(-1.3, -2.27) * mm, "end": v(-1.3, -2.25) * mm});
            skLineSegment(sketch, "E666", {"start": v(-1.3, -2.25) * mm, "end": v(-1.3, -2.23) * mm});
            skLineSegment(sketch, "E667", {"start": v(-1.3, -2.23) * mm, "end": v(-1.3, -2.17) * mm});
            skLineSegment(sketch, "E668", {"start": v(-1.3, -2.17) * mm, "end": v(-1.29, -2.1) * mm});
            skLineSegment(sketch, "E669", {"start": v(-1.29, -2.1) * mm, "end": v(-1.24, -2.04) * mm});
            skLineSegment(sketch, "E670", {"start": v(-1.24, -2.04) * mm, "end": v(-1.19, -2) * mm});
            skLineSegment(sketch, "E671", {"start": v(-1.19, -2) * mm, "end": v(-1.17, -2) * mm});
            skLineSegment(sketch, "E672", {"start": v(-1.17, -2) * mm, "end": v(-1.15, -2) * mm});
            skLineSegment(sketch, "E673", {"start": v(-1.15, -2) * mm, "end": v(-1.1, -1.99) * mm});
            skLineSegment(sketch, "E674", {"start": v(-1.1, -1.99) * mm, "end": v(-1.02, -2) * mm});
            skLineSegment(sketch, "E675", {"start": v(-1.02, -2) * mm, "end": v(-0.96, -2.06) * mm});
            skLineSegment(sketch, "E676", {"start": v(-0.96, -2.06) * mm, "end": v(-0.92, -2.1) * mm});
            skLineSegment(sketch, "E677", {"start": v(-0.92, -2.1) * mm, "end": v(-0.92, -2.13) * mm});
            skLineSegment(sketch, "E678", {"start": v(-0.92, -2.13) * mm, "end": v(-0.91, -2.15) * mm});
            skLineSegment(sketch, "E679", {"start": v(-0.91, -2.15) * mm, "end": v(-0.9, -2.2) * mm});
            skLineSegment(sketch, "E680", {"start": v(-0.9, -2.2) * mm, "end": v(-0.93, -2.28) * mm});
            skLineSegment(sketch, "E681", {"start": v(-0.93, -2.28) * mm, "end": v(-0.98, -2.34) * mm});
            skLineSegment(sketch, "E682", {"start": v(-0.98, -2.34) * mm, "end": v(-1.03, -2.37) * mm});
            skLineSegment(sketch, "E683", {"start": v(-1.03, -2.37) * mm, "end": v(-1.05, -2.38) * mm});
            skLineSegment(sketch, "E684", {"start": v(3.51, 0) * mm, "end": v(3.51, -0.09) * mm});
            skLineSegment(sketch, "E685", {"start": v(3.51, -0.09) * mm, "end": v(3.5, -0.36) * mm});
            skLineSegment(sketch, "E686", {"start": v(3.5, -0.36) * mm, "end": v(3.44, -0.7) * mm});
            skLineSegment(sketch, "E687", {"start": v(3.44, -0.7) * mm, "end": v(3.36, -1.04) * mm});
            skLineSegment(sketch, "E688", {"start": v(3.36, -1.04) * mm, "end": v(3.24, -1.37) * mm});
            skLineSegment(sketch, "E689", {"start": v(3.24, -1.37) * mm, "end": v(3.09, -1.67) * mm});
            skLineSegment(sketch, "E690", {"start": v(3.09, -1.67) * mm, "end": v(2.91, -1.96) * mm});
            skLineSegment(sketch, "E691", {"start": v(2.91, -1.96) * mm, "end": v(2.71, -2.24) * mm});
            skLineSegment(sketch, "E692", {"start": v(2.71, -2.24) * mm, "end": v(2.48, -2.48) * mm});
            skLineSegment(sketch, "E693", {"start": v(2.48, -2.48) * mm, "end": v(2.24, -2.71) * mm});
            skLineSegment(sketch, "E694", {"start": v(2.24, -2.71) * mm, "end": v(1.96, -2.91) * mm});
            skLineSegment(sketch, "E695", {"start": v(1.96, -2.91) * mm, "end": v(1.67, -3.09) * mm});
            skLineSegment(sketch, "E696", {"start": v(1.67, -3.09) * mm, "end": v(1.37, -3.24) * mm});
            skLineSegment(sketch, "E697", {"start": v(1.37, -3.24) * mm, "end": v(1.04, -3.36) * mm});
            skLineSegment(sketch, "E698", {"start": v(1.04, -3.36) * mm, "end": v(0.7, -3.44) * mm});
            skLineSegment(sketch, "E699", {"start": v(0.7, -3.44) * mm, "end": v(0.36, -3.5) * mm});
            skLineSegment(sketch, "E700", {"start": v(0.36, -3.5) * mm, "end": v(0.09, -3.51) * mm});
            skLineSegment(sketch, "E701", {"start": v(0.09, -3.51) * mm, "end": v(0, -3.51) * mm});
            skLineSegment(sketch, "E702", {"start": v(0, -3.51) * mm, "end": v(-0.09, -3.51) * mm});
            skLineSegment(sketch, "E703", {"start": v(-0.09, -3.51) * mm, "end": v(-0.36, -3.5) * mm});
            skLineSegment(sketch, "E704", {"start": v(-0.36, -3.5) * mm, "end": v(-0.7, -3.44) * mm});
            skLineSegment(sketch, "E705", {"start": v(-0.7, -3.44) * mm, "end": v(-1.04, -3.36) * mm});
            skLineSegment(sketch, "E706", {"start": v(-1.04, -3.36) * mm, "end": v(-1.37, -3.24) * mm});
            skLineSegment(sketch, "E707", {"start": v(-1.37, -3.24) * mm, "end": v(-1.67, -3.09) * mm});
            skLineSegment(sketch, "E708", {"start": v(-1.67, -3.09) * mm, "end": v(-1.96, -2.91) * mm});
            skLineSegment(sketch, "E709", {"start": v(-1.96, -2.91) * mm, "end": v(-2.24, -2.71) * mm});
            skLineSegment(sketch, "E710", {"start": v(-2.24, -2.71) * mm, "end": v(-2.48, -2.48) * mm});
            skLineSegment(sketch, "E711", {"start": v(-2.48, -2.48) * mm, "end": v(-2.71, -2.24) * mm});
            skLineSegment(sketch, "E712", {"start": v(-2.71, -2.24) * mm, "end": v(-2.91, -1.96) * mm});
            skLineSegment(sketch, "E713", {"start": v(-2.91, -1.96) * mm, "end": v(-3.09, -1.67) * mm});
            skLineSegment(sketch, "E714", {"start": v(-3.09, -1.67) * mm, "end": v(-3.24, -1.37) * mm});
            skLineSegment(sketch, "E715", {"start": v(-3.24, -1.37) * mm, "end": v(-3.36, -1.04) * mm});
            skLineSegment(sketch, "E716", {"start": v(-3.36, -1.04) * mm, "end": v(-3.44, -0.7) * mm});
            skLineSegment(sketch, "E717", {"start": v(-3.44, -0.7) * mm, "end": v(-3.5, -0.36) * mm});
            skLineSegment(sketch, "E718", {"start": v(-3.5, -0.36) * mm, "end": v(-3.51, -0.09) * mm});
            skLineSegment(sketch, "E719", {"start": v(-3.51, -0.09) * mm, "end": v(-3.51, 0) * mm});
            skLineSegment(sketch, "E720", {"start": v(-3.51, 0) * mm, "end": v(-3.51, 0.09) * mm});
            skLineSegment(sketch, "E721", {"start": v(-3.51, 0.09) * mm, "end": v(-3.5, 0.36) * mm});
            skLineSegment(sketch, "E722", {"start": v(-3.5, 0.36) * mm, "end": v(-3.44, 0.7) * mm});
            skLineSegment(sketch, "E723", {"start": v(-3.44, 0.7) * mm, "end": v(-3.36, 1.04) * mm});
            skLineSegment(sketch, "E724", {"start": v(-3.36, 1.04) * mm, "end": v(-3.24, 1.37) * mm});
            skLineSegment(sketch, "E725", {"start": v(-3.24, 1.37) * mm, "end": v(-3.09, 1.67) * mm});
            skLineSegment(sketch, "E726", {"start": v(-3.09, 1.67) * mm, "end": v(-2.91, 1.96) * mm});
            skLineSegment(sketch, "E727", {"start": v(-2.91, 1.96) * mm, "end": v(-2.71, 2.24) * mm});
            skLineSegment(sketch, "E728", {"start": v(-2.71, 2.24) * mm, "end": v(-2.48, 2.48) * mm});
            skLineSegment(sketch, "E729", {"start": v(-2.48, 2.48) * mm, "end": v(-2.24, 2.71) * mm});
            skLineSegment(sketch, "E730", {"start": v(-2.24, 2.71) * mm, "end": v(-1.96, 2.91) * mm});
            skLineSegment(sketch, "E731", {"start": v(-1.96, 2.91) * mm, "end": v(-1.67, 3.09) * mm});
            skLineSegment(sketch, "E732", {"start": v(-1.67, 3.09) * mm, "end": v(-1.37, 3.24) * mm});
            skLineSegment(sketch, "E733", {"start": v(-1.37, 3.24) * mm, "end": v(-1.04, 3.36) * mm});
            skLineSegment(sketch, "E734", {"start": v(-1.04, 3.36) * mm, "end": v(-0.7, 3.44) * mm});
            skLineSegment(sketch, "E735", {"start": v(-0.7, 3.44) * mm, "end": v(-0.36, 3.5) * mm});
            skLineSegment(sketch, "E736", {"start": v(-0.36, 3.5) * mm, "end": v(-0.09, 3.51) * mm});
            skLineSegment(sketch, "E737", {"start": v(-0.09, 3.51) * mm, "end": v(0, 3.51) * mm});
            skLineSegment(sketch, "E738", {"start": v(0, 3.51) * mm, "end": v(0.09, 3.51) * mm});
            skLineSegment(sketch, "E739", {"start": v(0.09, 3.51) * mm, "end": v(0.36, 3.5) * mm});
            skLineSegment(sketch, "E740", {"start": v(0.36, 3.5) * mm, "end": v(0.7, 3.44) * mm});
            skLineSegment(sketch, "E741", {"start": v(0.7, 3.44) * mm, "end": v(1.04, 3.36) * mm});
            skLineSegment(sketch, "E742", {"start": v(1.04, 3.36) * mm, "end": v(1.37, 3.24) * mm});
            skLineSegment(sketch, "E743", {"start": v(1.37, 3.24) * mm, "end": v(1.67, 3.09) * mm});
            skLineSegment(sketch, "E744", {"start": v(1.67, 3.09) * mm, "end": v(1.96, 2.91) * mm});
            skLineSegment(sketch, "E745", {"start": v(1.96, 2.91) * mm, "end": v(2.24, 2.71) * mm});
            skLineSegment(sketch, "E746", {"start": v(2.24, 2.71) * mm, "end": v(2.48, 2.48) * mm});
            skLineSegment(sketch, "E747", {"start": v(2.48, 2.48) * mm, "end": v(2.71, 2.24) * mm});
            skLineSegment(sketch, "E748", {"start": v(2.71, 2.24) * mm, "end": v(2.91, 1.96) * mm});
            skLineSegment(sketch, "E749", {"start": v(2.91, 1.96) * mm, "end": v(3.09, 1.67) * mm});
            skLineSegment(sketch, "E750", {"start": v(3.09, 1.67) * mm, "end": v(3.24, 1.37) * mm});
            skLineSegment(sketch, "E751", {"start": v(3.24, 1.37) * mm, "end": v(3.36, 1.04) * mm});
            skLineSegment(sketch, "E752", {"start": v(3.36, 1.04) * mm, "end": v(3.44, 0.7) * mm});
            skLineSegment(sketch, "E753", {"start": v(3.44, 0.7) * mm, "end": v(3.5, 0.36) * mm});
            skLineSegment(sketch, "E754", {"start": v(3.5, 0.36) * mm, "end": v(3.51, 0.09) * mm});
            skLineSegment(sketch, "E755", {"start": v(3.51, 0.09) * mm, "end": v(3.51, 0) * mm});
            skSolve(sketch);
        }
        {
            var Q0;
            {var subQ0=sQuery(id+"F0.wireOp",EDGE,"E29");Q0=makeQuery(id+"F0.imprint","IMPRINT",FACE,{"disambiguationData":[TD([[makeQuery(id+"F0.imprint","IMPRINT",EDGE,{"derivedFrom":subQ0}),-1.0]])]});}
            var Q1;
            Q1=makeQuery(id+"F0.imprint","IMPRINT",FACE,{"disambiguationData":[TD([[makeQuery(id+"F0.imprint","IMPRINT",EDGE,{"derivedFrom":sQuery(id+"F0.wireOp",EDGE,"E0")}),-1.0]])]});
            var Q2;
            {var subQ5=sQuery(id+"F0.wireOp",EDGE,"E61");Q2=makeQuery(id+"F0.imprint","IMPRINT",FACE,{"disambiguationData":[TD([[makeQuery(id+"F0.imprint","IMPRINT",EDGE,{"derivedFrom":subQ5}),-1.0]])]});}
            extrude(context, id + "F1", {"entities" : qUnion([Q0, Q1, Q2]), "depth" : 0.4 * mm});
        }
        {
            var Q0;
            Q0=makeQuery(id+"F0.imprint","IMPRINT",FACE,{"disambiguationData":[TD([[makeQuery(id+"F0.imprint","IMPRINT",EDGE,{"derivedFrom":sQuery(id+"F0.wireOp",EDGE,"E0")}),1.0]])]});
            var Q1;
            Q1=makeQuery(id+"F0.imprint","IMPRINT",FACE,{"disambiguationData":[TD([[makeQuery(id+"F0.imprint","IMPRINT",EDGE,{"derivedFrom":sQuery(id+"F0.wireOp",EDGE,"E156")}),-1.0]])]});
            var Q2;
            Q2=makeQuery(id+"F0.imprint","IMPRINT",FACE,{"disambiguationData":[TD([[makeQuery(id+"F0.imprint","IMPRINT",EDGE,{"derivedFrom":sQuery(id+"F0.wireOp",EDGE,"E0")}),-1.0]])]});
            extrude(context, id + "F2", {"entities" : qUnion([Q0, Q1, Q2]), "depth" : 0.4 * mm});
        }
        {
            var Q0;
            Q0=makeQuery(id+"F0.imprint","IMPRINT",FACE,{"disambiguationData":[TD([[makeQuery(id+"F0.imprint","IMPRINT",EDGE,{"derivedFrom":sQuery(id+"F0.wireOp",EDGE,"E156")}),1.0]])]});
            var Q1;
            Q1=makeQuery(id+"F0.imprint","IMPRINT",FACE,{"disambiguationData":[TD([[makeQuery(id+"F0.imprint","IMPRINT",EDGE,{"derivedFrom":sQuery(id+"F0.wireOp",EDGE,"E280")}),-1.0]])]});
            var Q2;
            Q2=makeQuery(id+"F0.imprint","IMPRINT",FACE,{"disambiguationData":[TD([[makeQuery(id+"F0.imprint","IMPRINT",EDGE,{"derivedFrom":sQuery(id+"F0.wireOp",EDGE,"E156")}),-1.0]])]});
            extrude(context, id + "F3", {"entities" : qUnion([Q0, Q1, Q2]), "depth" : 0.4 * mm});
        }
        {
            var Q0;
            Q0=makeQuery(id+"F0.imprint","IMPRINT",FACE,{"disambiguationData":[TD([[makeQuery(id+"F0.imprint","IMPRINT",EDGE,{"derivedFrom":sQuery(id+"F0.wireOp",EDGE,"E280")}),1.0]])]});
            var Q1;
            Q1=makeQuery(id+"F0.imprint","IMPRINT",FACE,{"disambiguationData":[TD([[makeQuery(id+"F0.imprint","IMPRINT",EDGE,{"derivedFrom":sQuery(id+"F0.wireOp",EDGE,"E404")}),-1.0]])]});
            var Q2;
            Q2=makeQuery(id+"F0.imprint","IMPRINT",FACE,{"disambiguationData":[TD([[makeQuery(id+"F0.imprint","IMPRINT",EDGE,{"derivedFrom":sQuery(id+"F0.wireOp",EDGE,"E280")}),-1.0]])]});
            extrude(context, id + "F4", {"entities" : qUnion([Q0, Q1, Q2]), "depth" : 0.4 * mm});
        }
        {
            var Q0;
            {var subQ0=sQuery(id+"F0.wireOp",EDGE,"E61");Q0=makeQuery(id+"F0.imprint","IMPRINT",FACE,{"disambiguationData":[TD([[makeQuery(id+"F0.imprint","IMPRINT",EDGE,{"derivedFrom":subQ0}),1.0]])]});}
            var Q1;
            Q1=makeQuery(id+"F0.imprint","IMPRINT",FACE,{"disambiguationData":[TD([[makeQuery(id+"F0.imprint","IMPRINT",EDGE,{"derivedFrom":sQuery(id+"F0.wireOp",EDGE,"E404")}),-1.0]])]});
            var Q2;
            {var subQ5=sQuery(id+"F0.wireOp",EDGE,"E61");Q2=makeQuery(id+"F0.imprint","IMPRINT",FACE,{"disambiguationData":[TD([[makeQuery(id+"F0.imprint","IMPRINT",EDGE,{"derivedFrom":subQ5}),-1.0]])]});}
            extrude(context, id + "F5", {"entities" : qUnion([Q0, Q1, Q2]), "depth" : 0.4 * mm});
        }
        {
            var Q0;
            Q0=makeQuery(id+"F5.opExtrude","SWEPT_BODY",BODY,{"disambiguationData":[OSD([sQuery(id+"F0.wireOp",EDGE,"E544"),sQuery(id+"F0.wireOp",EDGE,"E545"),sQuery(id+"F0.wireOp",EDGE,"E546"),sQuery(id+"F0.wireOp",EDGE,"E547"),sQuery(id+"F0.wireOp",EDGE,"E548"),sQuery(id+"F0.wireOp",EDGE,"E549"),sQuery(id+"F0.wireOp",EDGE,"E550"),sQuery(id+"F0.wireOp",EDGE,"E551"),sQuery(id+"F0.wireOp",EDGE,"E552"),sQuery(id+"F0.wireOp",EDGE,"E553"),sQuery(id+"F0.wireOp",EDGE,"E554"),sQuery(id+"F0.wireOp",EDGE,"E555"),sQuery(id+"F0.wireOp",EDGE,"E556"),sQuery(id+"F0.wireOp",EDGE,"E557"),sQuery(id+"F0.wireOp",EDGE,"E558"),sQuery(id+"F0.wireOp",EDGE,"E559"),sQuery(id+"F0.wireOp",EDGE,"E560"),sQuery(id+"F0.wireOp",EDGE,"E561"),sQuery(id+"F0.wireOp",EDGE,"E562"),sQuery(id+"F0.wireOp",EDGE,"E563"),sQuery(id+"F0.wireOp",EDGE,"E564"),sQuery(id+"F0.wireOp",EDGE,"E565"),sQuery(id+"F0.wireOp",EDGE,"E566"),sQuery(id+"F0.wireOp",EDGE,"E567"),sQuery(id+"F0.wireOp",EDGE,"E568"),sQuery(id+"F0.wireOp",EDGE,"E569"),sQuery(id+"F0.wireOp",EDGE,"E570"),sQuery(id+"F0.wireOp",EDGE,"E571"),sQuery(id+"F0.wireOp",EDGE,"E572"),sQuery(id+"F0.wireOp",EDGE,"E573"),sQuery(id+"F0.wireOp",EDGE,"E574"),sQuery(id+"F0.wireOp",EDGE,"E575"),sQuery(id+"F0.wireOp",EDGE,"E576"),sQuery(id+"F0.wireOp",EDGE,"E577"),sQuery(id+"F0.wireOp",EDGE,"E578"),sQuery(id+"F0.wireOp",EDGE,"E579"),sQuery(id+"F0.wireOp",EDGE,"E580"),sQuery(id+"F0.wireOp",EDGE,"E581"),sQuery(id+"F0.wireOp",EDGE,"E582"),sQuery(id+"F0.wireOp",EDGE,"E583"),sQuery(id+"F0.wireOp",EDGE,"E584"),sQuery(id+"F0.wireOp",EDGE,"E585"),sQuery(id+"F0.wireOp",EDGE,"E586"),sQuery(id+"F0.wireOp",EDGE,"E587"),sQuery(id+"F0.wireOp",EDGE,"E588"),sQuery(id+"F0.wireOp",EDGE,"E589"),sQuery(id+"F0.wireOp",EDGE,"E590"),sQuery(id+"F0.wireOp",EDGE,"E591"),sQuery(id+"F0.wireOp",EDGE,"E592"),sQuery(id+"F0.wireOp",EDGE,"E593"),sQuery(id+"F0.wireOp",EDGE,"E594"),sQuery(id+"F0.wireOp",EDGE,"E595"),sQuery(id+"F0.wireOp",EDGE,"E596"),sQuery(id+"F0.wireOp",EDGE,"E597"),sQuery(id+"F0.wireOp",EDGE,"E598"),sQuery(id+"F0.wireOp",EDGE,"E599"),sQuery(id+"F0.wireOp",EDGE,"E600"),sQuery(id+"F0.wireOp",EDGE,"E601"),sQuery(id+"F0.wireOp",EDGE,"E602"),sQuery(id+"F0.wireOp",EDGE,"E603"),sQuery(id+"F0.wireOp",EDGE,"E604"),sQuery(id+"F0.wireOp",EDGE,"E605"),sQuery(id+"F0.wireOp",EDGE,"E606"),sQuery(id+"F0.wireOp",EDGE,"E607"),sQuery(id+"F0.wireOp",EDGE,"E608"),sQuery(id+"F0.wireOp",EDGE,"E609"),sQuery(id+"F0.wireOp",EDGE,"E610"),sQuery(id+"F0.wireOp",EDGE,"E611"),sQuery(id+"F0.wireOp",EDGE,"E612"),sQuery(id+"F0.wireOp",EDGE,"E613"),sQuery(id+"F0.wireOp",EDGE,"E614"),sQuery(id+"F0.wireOp",EDGE,"E615"),sQuery(id+"F0.wireOp",EDGE,"E616"),sQuery(id+"F0.wireOp",EDGE,"E617"),sQuery(id+"F0.wireOp",EDGE,"E618"),sQuery(id+"F0.wireOp",EDGE,"E619"),sQuery(id+"F0.wireOp",EDGE,"E620"),sQuery(id+"F0.wireOp",EDGE,"E621"),sQuery(id+"F0.wireOp",EDGE,"E622"),sQuery(id+"F0.wireOp",EDGE,"E623"),sQuery(id+"F0.wireOp",EDGE,"E624"),sQuery(id+"F0.wireOp",EDGE,"E625"),sQuery(id+"F0.wireOp",EDGE,"E626"),sQuery(id+"F0.wireOp",EDGE,"E627"),sQuery(id+"F0.wireOp",EDGE,"E628"),sQuery(id+"F0.wireOp",EDGE,"E629"),sQuery(id+"F0.wireOp",EDGE,"E630"),sQuery(id+"F0.wireOp",EDGE,"E631"),sQuery(id+"F0.wireOp",EDGE,"E632"),sQuery(id+"F0.wireOp",EDGE,"E633"),sQuery(id+"F0.wireOp",EDGE,"E634"),sQuery(id+"F0.wireOp",EDGE,"E635"),sQuery(id+"F0.wireOp",EDGE,"E636"),sQuery(id+"F0.wireOp",EDGE,"E637"),sQuery(id+"F0.wireOp",EDGE,"E638"),sQuery(id+"F0.wireOp",EDGE,"E639"),sQuery(id+"F0.wireOp",EDGE,"E640"),sQuery(id+"F0.wireOp",EDGE,"E641"),sQuery(id+"F0.wireOp",EDGE,"E642"),sQuery(id+"F0.wireOp",EDGE,"E643"),sQuery(id+"F0.wireOp",EDGE,"E644"),sQuery(id+"F0.wireOp",EDGE,"E645"),sQuery(id+"F0.wireOp",EDGE,"E646"),sQuery(id+"F0.wireOp",EDGE,"E647"),sQuery(id+"F0.wireOp",EDGE,"E648"),sQuery(id+"F0.wireOp",EDGE,"E649"),sQuery(id+"F0.wireOp",EDGE,"E650"),sQuery(id+"F0.wireOp",EDGE,"E651"),sQuery(id+"F0.wireOp",EDGE,"E652"),sQuery(id+"F0.wireOp",EDGE,"E653"),sQuery(id+"F0.wireOp",EDGE,"E654"),sQuery(id+"F0.wireOp",EDGE,"E655"),sQuery(id+"F0.wireOp",EDGE,"E656"),sQuery(id+"F0.wireOp",EDGE,"E657"),sQuery(id+"F0.wireOp",EDGE,"E658"),sQuery(id+"F0.wireOp",EDGE,"E659"),sQuery(id+"F0.wireOp",EDGE,"E660"),sQuery(id+"F0.wireOp",EDGE,"E661"),sQuery(id+"F0.wireOp",EDGE,"E662"),sQuery(id+"F0.wireOp",EDGE,"E663"),sQuery(id+"F0.wireOp",EDGE,"E664"),sQuery(id+"F0.wireOp",EDGE,"E665"),sQuery(id+"F0.wireOp",EDGE,"E666"),sQuery(id+"F0.wireOp",EDGE,"E667"),sQuery(id+"F0.wireOp",EDGE,"E668"),sQuery(id+"F0.wireOp",EDGE,"E669"),sQuery(id+"F0.wireOp",EDGE,"E670"),sQuery(id+"F0.wireOp",EDGE,"E671"),sQuery(id+"F0.wireOp",EDGE,"E672"),sQuery(id+"F0.wireOp",EDGE,"E673"),sQuery(id+"F0.wireOp",EDGE,"E674"),sQuery(id+"F0.wireOp",EDGE,"E675"),sQuery(id+"F0.wireOp",EDGE,"E676"),sQuery(id+"F0.wireOp",EDGE,"E677"),sQuery(id+"F0.wireOp",EDGE,"E678"),sQuery(id+"F0.wireOp",EDGE,"E679"),sQuery(id+"F0.wireOp",EDGE,"E680"),sQuery(id+"F0.wireOp",EDGE,"E681"),sQuery(id+"F0.wireOp",EDGE,"E682"),sQuery(id+"F0.wireOp",EDGE,"E683")])]});
            transform(context, id + "F6", {"entities" : qUnion([Q0]), "transformType" : TransformType.TRANSLATION_3D, "dx" : 0 * mm, "dy" : 0.4 * mm, "dz" : 0 * mm, "makeCopy" : false});
        }
        {
            var Q0;
            Q0=makeQuery(id+"F4.opExtrude","SWEPT_BODY",BODY,{"disambiguationData":[OSD([sQuery(id+"F0.wireOp",EDGE,"E404"),sQuery(id+"F0.wireOp",EDGE,"E405"),sQuery(id+"F0.wireOp",EDGE,"E406"),sQuery(id+"F0.wireOp",EDGE,"E407"),sQuery(id+"F0.wireOp",EDGE,"E408"),sQuery(id+"F0.wireOp",EDGE,"E409"),sQuery(id+"F0.wireOp",EDGE,"E410"),sQuery(id+"F0.wireOp",EDGE,"E411"),sQuery(id+"F0.wireOp",EDGE,"E412"),sQuery(id+"F0.wireOp",EDGE,"E413"),sQuery(id+"F0.wireOp",EDGE,"E414"),sQuery(id+"F0.wireOp",EDGE,"E415"),sQuery(id+"F0.wireOp",EDGE,"E416"),sQuery(id+"F0.wireOp",EDGE,"E417"),sQuery(id+"F0.wireOp",EDGE,"E418"),sQuery(id+"F0.wireOp",EDGE,"E419"),sQuery(id+"F0.wireOp",EDGE,"E420"),sQuery(id+"F0.wireOp",EDGE,"E421"),sQuery(id+"F0.wireOp",EDGE,"E422"),sQuery(id+"F0.wireOp",EDGE,"E423"),sQuery(id+"F0.wireOp",EDGE,"E424"),sQuery(id+"F0.wireOp",EDGE,"E425"),sQuery(id+"F0.wireOp",EDGE,"E426"),sQuery(id+"F0.wireOp",EDGE,"E427"),sQuery(id+"F0.wireOp",EDGE,"E428"),sQuery(id+"F0.wireOp",EDGE,"E429"),sQuery(id+"F0.wireOp",EDGE,"E430"),sQuery(id+"F0.wireOp",EDGE,"E431"),sQuery(id+"F0.wireOp",EDGE,"E432"),sQuery(id+"F0.wireOp",EDGE,"E433"),sQuery(id+"F0.wireOp",EDGE,"E434"),sQuery(id+"F0.wireOp",EDGE,"E435"),sQuery(id+"F0.wireOp",EDGE,"E436"),sQuery(id+"F0.wireOp",EDGE,"E437"),sQuery(id+"F0.wireOp",EDGE,"E438"),sQuery(id+"F0.wireOp",EDGE,"E439"),sQuery(id+"F0.wireOp",EDGE,"E440"),sQuery(id+"F0.wireOp",EDGE,"E441"),sQuery(id+"F0.wireOp",EDGE,"E442"),sQuery(id+"F0.wireOp",EDGE,"E443"),sQuery(id+"F0.wireOp",EDGE,"E444"),sQuery(id+"F0.wireOp",EDGE,"E445"),sQuery(id+"F0.wireOp",EDGE,"E446"),sQuery(id+"F0.wireOp",EDGE,"E447"),sQuery(id+"F0.wireOp",EDGE,"E448"),sQuery(id+"F0.wireOp",EDGE,"E449"),sQuery(id+"F0.wireOp",EDGE,"E450"),sQuery(id+"F0.wireOp",EDGE,"E451"),sQuery(id+"F0.wireOp",EDGE,"E452"),sQuery(id+"F0.wireOp",EDGE,"E453"),sQuery(id+"F0.wireOp",EDGE,"E454"),sQuery(id+"F0.wireOp",EDGE,"E455"),sQuery(id+"F0.wireOp",EDGE,"E456"),sQuery(id+"F0.wireOp",EDGE,"E457"),sQuery(id+"F0.wireOp",EDGE,"E458"),sQuery(id+"F0.wireOp",EDGE,"E459"),sQuery(id+"F0.wireOp",EDGE,"E460"),sQuery(id+"F0.wireOp",EDGE,"E461"),sQuery(id+"F0.wireOp",EDGE,"E462"),sQuery(id+"F0.wireOp",EDGE,"E463"),sQuery(id+"F0.wireOp",EDGE,"E464"),sQuery(id+"F0.wireOp",EDGE,"E465"),sQuery(id+"F0.wireOp",EDGE,"E466"),sQuery(id+"F0.wireOp",EDGE,"E467"),sQuery(id+"F0.wireOp",EDGE,"E468"),sQuery(id+"F0.wireOp",EDGE,"E469"),sQuery(id+"F0.wireOp",EDGE,"E470"),sQuery(id+"F0.wireOp",EDGE,"E471"),sQuery(id+"F0.wireOp",EDGE,"E472"),sQuery(id+"F0.wireOp",EDGE,"E473"),sQuery(id+"F0.wireOp",EDGE,"E474"),sQuery(id+"F0.wireOp",EDGE,"E475"),sQuery(id+"F0.wireOp",EDGE,"E476"),sQuery(id+"F0.wireOp",EDGE,"E477"),sQuery(id+"F0.wireOp",EDGE,"E478"),sQuery(id+"F0.wireOp",EDGE,"E479"),sQuery(id+"F0.wireOp",EDGE,"E480"),sQuery(id+"F0.wireOp",EDGE,"E481"),sQuery(id+"F0.wireOp",EDGE,"E482"),sQuery(id+"F0.wireOp",EDGE,"E483"),sQuery(id+"F0.wireOp",EDGE,"E484"),sQuery(id+"F0.wireOp",EDGE,"E485"),sQuery(id+"F0.wireOp",EDGE,"E486"),sQuery(id+"F0.wireOp",EDGE,"E487"),sQuery(id+"F0.wireOp",EDGE,"E488"),sQuery(id+"F0.wireOp",EDGE,"E489"),sQuery(id+"F0.wireOp",EDGE,"E490"),sQuery(id+"F0.wireOp",EDGE,"E491"),sQuery(id+"F0.wireOp",EDGE,"E492"),sQuery(id+"F0.wireOp",EDGE,"E493"),sQuery(id+"F0.wireOp",EDGE,"E494"),sQuery(id+"F0.wireOp",EDGE,"E495"),sQuery(id+"F0.wireOp",EDGE,"E496"),sQuery(id+"F0.wireOp",EDGE,"E497"),sQuery(id+"F0.wireOp",EDGE,"E498"),sQuery(id+"F0.wireOp",EDGE,"E499"),sQuery(id+"F0.wireOp",EDGE,"E500"),sQuery(id+"F0.wireOp",EDGE,"E501"),sQuery(id+"F0.wireOp",EDGE,"E502"),sQuery(id+"F0.wireOp",EDGE,"E503"),sQuery(id+"F0.wireOp",EDGE,"E504"),sQuery(id+"F0.wireOp",EDGE,"E505"),sQuery(id+"F0.wireOp",EDGE,"E506"),sQuery(id+"F0.wireOp",EDGE,"E507"),sQuery(id+"F0.wireOp",EDGE,"E508"),sQuery(id+"F0.wireOp",EDGE,"E509"),sQuery(id+"F0.wireOp",EDGE,"E510"),sQuery(id+"F0.wireOp",EDGE,"E511"),sQuery(id+"F0.wireOp",EDGE,"E512"),sQuery(id+"F0.wireOp",EDGE,"E513"),sQuery(id+"F0.wireOp",EDGE,"E514"),sQuery(id+"F0.wireOp",EDGE,"E515"),sQuery(id+"F0.wireOp",EDGE,"E516"),sQuery(id+"F0.wireOp",EDGE,"E517"),sQuery(id+"F0.wireOp",EDGE,"E518"),sQuery(id+"F0.wireOp",EDGE,"E519"),sQuery(id+"F0.wireOp",EDGE,"E520"),sQuery(id+"F0.wireOp",EDGE,"E521"),sQuery(id+"F0.wireOp",EDGE,"E522"),sQuery(id+"F0.wireOp",EDGE,"E523"),sQuery(id+"F0.wireOp",EDGE,"E524"),sQuery(id+"F0.wireOp",EDGE,"E525"),sQuery(id+"F0.wireOp",EDGE,"E526"),sQuery(id+"F0.wireOp",EDGE,"E527"),sQuery(id+"F0.wireOp",EDGE,"E528"),sQuery(id+"F0.wireOp",EDGE,"E529"),sQuery(id+"F0.wireOp",EDGE,"E530"),sQuery(id+"F0.wireOp",EDGE,"E531"),sQuery(id+"F0.wireOp",EDGE,"E532"),sQuery(id+"F0.wireOp",EDGE,"E533"),sQuery(id+"F0.wireOp",EDGE,"E534"),sQuery(id+"F0.wireOp",EDGE,"E535"),sQuery(id+"F0.wireOp",EDGE,"E536"),sQuery(id+"F0.wireOp",EDGE,"E537"),sQuery(id+"F0.wireOp",EDGE,"E538"),sQuery(id+"F0.wireOp",EDGE,"E539"),sQuery(id+"F0.wireOp",EDGE,"E540"),sQuery(id+"F0.wireOp",EDGE,"E541"),sQuery(id+"F0.wireOp",EDGE,"E542"),sQuery(id+"F0.wireOp",EDGE,"E543")])]});
            transform(context, id + "F7", {"entities" : qUnion([Q0]), "transformType" : TransformType.TRANSLATION_3D, "dx" : 0 * mm, "dy" : 0.8 * mm, "dz" : 0 * mm, "makeCopy" : false});
        }
        {
            var Q0;
            Q0=makeQuery(id+"F3.opExtrude","SWEPT_BODY",BODY,{"disambiguationData":[OSD([sQuery(id+"F0.wireOp",EDGE,"E280"),sQuery(id+"F0.wireOp",EDGE,"E281"),sQuery(id+"F0.wireOp",EDGE,"E282"),sQuery(id+"F0.wireOp",EDGE,"E283"),sQuery(id+"F0.wireOp",EDGE,"E284"),sQuery(id+"F0.wireOp",EDGE,"E285"),sQuery(id+"F0.wireOp",EDGE,"E286"),sQuery(id+"F0.wireOp",EDGE,"E287"),sQuery(id+"F0.wireOp",EDGE,"E288"),sQuery(id+"F0.wireOp",EDGE,"E289"),sQuery(id+"F0.wireOp",EDGE,"E290"),sQuery(id+"F0.wireOp",EDGE,"E291"),sQuery(id+"F0.wireOp",EDGE,"E292"),sQuery(id+"F0.wireOp",EDGE,"E293"),sQuery(id+"F0.wireOp",EDGE,"E294"),sQuery(id+"F0.wireOp",EDGE,"E295"),sQuery(id+"F0.wireOp",EDGE,"E296"),sQuery(id+"F0.wireOp",EDGE,"E297"),sQuery(id+"F0.wireOp",EDGE,"E298"),sQuery(id+"F0.wireOp",EDGE,"E299"),sQuery(id+"F0.wireOp",EDGE,"E300"),sQuery(id+"F0.wireOp",EDGE,"E301"),sQuery(id+"F0.wireOp",EDGE,"E302"),sQuery(id+"F0.wireOp",EDGE,"E303"),sQuery(id+"F0.wireOp",EDGE,"E304"),sQuery(id+"F0.wireOp",EDGE,"E305"),sQuery(id+"F0.wireOp",EDGE,"E306"),sQuery(id+"F0.wireOp",EDGE,"E307"),sQuery(id+"F0.wireOp",EDGE,"E308"),sQuery(id+"F0.wireOp",EDGE,"E309"),sQuery(id+"F0.wireOp",EDGE,"E310"),sQuery(id+"F0.wireOp",EDGE,"E311"),sQuery(id+"F0.wireOp",EDGE,"E312"),sQuery(id+"F0.wireOp",EDGE,"E313"),sQuery(id+"F0.wireOp",EDGE,"E314"),sQuery(id+"F0.wireOp",EDGE,"E315"),sQuery(id+"F0.wireOp",EDGE,"E316"),sQuery(id+"F0.wireOp",EDGE,"E317"),sQuery(id+"F0.wireOp",EDGE,"E318"),sQuery(id+"F0.wireOp",EDGE,"E319"),sQuery(id+"F0.wireOp",EDGE,"E320"),sQuery(id+"F0.wireOp",EDGE,"E321"),sQuery(id+"F0.wireOp",EDGE,"E322"),sQuery(id+"F0.wireOp",EDGE,"E323"),sQuery(id+"F0.wireOp",EDGE,"E324"),sQuery(id+"F0.wireOp",EDGE,"E325"),sQuery(id+"F0.wireOp",EDGE,"E326"),sQuery(id+"F0.wireOp",EDGE,"E327"),sQuery(id+"F0.wireOp",EDGE,"E328"),sQuery(id+"F0.wireOp",EDGE,"E329"),sQuery(id+"F0.wireOp",EDGE,"E330"),sQuery(id+"F0.wireOp",EDGE,"E331"),sQuery(id+"F0.wireOp",EDGE,"E332"),sQuery(id+"F0.wireOp",EDGE,"E333"),sQuery(id+"F0.wireOp",EDGE,"E334"),sQuery(id+"F0.wireOp",EDGE,"E335"),sQuery(id+"F0.wireOp",EDGE,"E336"),sQuery(id+"F0.wireOp",EDGE,"E337"),sQuery(id+"F0.wireOp",EDGE,"E338"),sQuery(id+"F0.wireOp",EDGE,"E339"),sQuery(id+"F0.wireOp",EDGE,"E340"),sQuery(id+"F0.wireOp",EDGE,"E341"),sQuery(id+"F0.wireOp",EDGE,"E342"),sQuery(id+"F0.wireOp",EDGE,"E343"),sQuery(id+"F0.wireOp",EDGE,"E344"),sQuery(id+"F0.wireOp",EDGE,"E345"),sQuery(id+"F0.wireOp",EDGE,"E346"),sQuery(id+"F0.wireOp",EDGE,"E347"),sQuery(id+"F0.wireOp",EDGE,"E348"),sQuery(id+"F0.wireOp",EDGE,"E349"),sQuery(id+"F0.wireOp",EDGE,"E350"),sQuery(id+"F0.wireOp",EDGE,"E351"),sQuery(id+"F0.wireOp",EDGE,"E352"),sQuery(id+"F0.wireOp",EDGE,"E353"),sQuery(id+"F0.wireOp",EDGE,"E354"),sQuery(id+"F0.wireOp",EDGE,"E355"),sQuery(id+"F0.wireOp",EDGE,"E356"),sQuery(id+"F0.wireOp",EDGE,"E357"),sQuery(id+"F0.wireOp",EDGE,"E358"),sQuery(id+"F0.wireOp",EDGE,"E359"),sQuery(id+"F0.wireOp",EDGE,"E360"),sQuery(id+"F0.wireOp",EDGE,"E361"),sQuery(id+"F0.wireOp",EDGE,"E362"),sQuery(id+"F0.wireOp",EDGE,"E363"),sQuery(id+"F0.wireOp",EDGE,"E364"),sQuery(id+"F0.wireOp",EDGE,"E365"),sQuery(id+"F0.wireOp",EDGE,"E366"),sQuery(id+"F0.wireOp",EDGE,"E367"),sQuery(id+"F0.wireOp",EDGE,"E368"),sQuery(id+"F0.wireOp",EDGE,"E369"),sQuery(id+"F0.wireOp",EDGE,"E370"),sQuery(id+"F0.wireOp",EDGE,"E371"),sQuery(id+"F0.wireOp",EDGE,"E372"),sQuery(id+"F0.wireOp",EDGE,"E373"),sQuery(id+"F0.wireOp",EDGE,"E374"),sQuery(id+"F0.wireOp",EDGE,"E375"),sQuery(id+"F0.wireOp",EDGE,"E376"),sQuery(id+"F0.wireOp",EDGE,"E377"),sQuery(id+"F0.wireOp",EDGE,"E378"),sQuery(id+"F0.wireOp",EDGE,"E379"),sQuery(id+"F0.wireOp",EDGE,"E380"),sQuery(id+"F0.wireOp",EDGE,"E381"),sQuery(id+"F0.wireOp",EDGE,"E382"),sQuery(id+"F0.wireOp",EDGE,"E383"),sQuery(id+"F0.wireOp",EDGE,"E384"),sQuery(id+"F0.wireOp",EDGE,"E385"),sQuery(id+"F0.wireOp",EDGE,"E386"),sQuery(id+"F0.wireOp",EDGE,"E387"),sQuery(id+"F0.wireOp",EDGE,"E388"),sQuery(id+"F0.wireOp",EDGE,"E389"),sQuery(id+"F0.wireOp",EDGE,"E390"),sQuery(id+"F0.wireOp",EDGE,"E391"),sQuery(id+"F0.wireOp",EDGE,"E392"),sQuery(id+"F0.wireOp",EDGE,"E393"),sQuery(id+"F0.wireOp",EDGE,"E394"),sQuery(id+"F0.wireOp",EDGE,"E395"),sQuery(id+"F0.wireOp",EDGE,"E396"),sQuery(id+"F0.wireOp",EDGE,"E397"),sQuery(id+"F0.wireOp",EDGE,"E398"),sQuery(id+"F0.wireOp",EDGE,"E399"),sQuery(id+"F0.wireOp",EDGE,"E400"),sQuery(id+"F0.wireOp",EDGE,"E401"),sQuery(id+"F0.wireOp",EDGE,"E402"),sQuery(id+"F0.wireOp",EDGE,"E403")])]});
            transform(context, id + "F8", {"entities" : qUnion([Q0]), "transformType" : TransformType.TRANSLATION_3D, "dx" : 0 * mm, "dy" : 0.4 * mm, "dz" : 0 * mm, "makeCopy" : false});
        }
        {
            var Q0;
            Q0=makeQuery(id+"F2.opExtrude","SWEPT_BODY",BODY,{"disambiguationData":[OSD([sQuery(id+"F0.wireOp",EDGE,"E156"),sQuery(id+"F0.wireOp",EDGE,"E157"),sQuery(id+"F0.wireOp",EDGE,"E158"),sQuery(id+"F0.wireOp",EDGE,"E159"),sQuery(id+"F0.wireOp",EDGE,"E160"),sQuery(id+"F0.wireOp",EDGE,"E161"),sQuery(id+"F0.wireOp",EDGE,"E162"),sQuery(id+"F0.wireOp",EDGE,"E163"),sQuery(id+"F0.wireOp",EDGE,"E164"),sQuery(id+"F0.wireOp",EDGE,"E165"),sQuery(id+"F0.wireOp",EDGE,"E166"),sQuery(id+"F0.wireOp",EDGE,"E167"),sQuery(id+"F0.wireOp",EDGE,"E168"),sQuery(id+"F0.wireOp",EDGE,"E169"),sQuery(id+"F0.wireOp",EDGE,"E170"),sQuery(id+"F0.wireOp",EDGE,"E171"),sQuery(id+"F0.wireOp",EDGE,"E172"),sQuery(id+"F0.wireOp",EDGE,"E173"),sQuery(id+"F0.wireOp",EDGE,"E174"),sQuery(id+"F0.wireOp",EDGE,"E175"),sQuery(id+"F0.wireOp",EDGE,"E176"),sQuery(id+"F0.wireOp",EDGE,"E177"),sQuery(id+"F0.wireOp",EDGE,"E178"),sQuery(id+"F0.wireOp",EDGE,"E179"),sQuery(id+"F0.wireOp",EDGE,"E180"),sQuery(id+"F0.wireOp",EDGE,"E181"),sQuery(id+"F0.wireOp",EDGE,"E182"),sQuery(id+"F0.wireOp",EDGE,"E183"),sQuery(id+"F0.wireOp",EDGE,"E184"),sQuery(id+"F0.wireOp",EDGE,"E185"),sQuery(id+"F0.wireOp",EDGE,"E186"),sQuery(id+"F0.wireOp",EDGE,"E187"),sQuery(id+"F0.wireOp",EDGE,"E188"),sQuery(id+"F0.wireOp",EDGE,"E189"),sQuery(id+"F0.wireOp",EDGE,"E190"),sQuery(id+"F0.wireOp",EDGE,"E191"),sQuery(id+"F0.wireOp",EDGE,"E192"),sQuery(id+"F0.wireOp",EDGE,"E193"),sQuery(id+"F0.wireOp",EDGE,"E194"),sQuery(id+"F0.wireOp",EDGE,"E195"),sQuery(id+"F0.wireOp",EDGE,"E196"),sQuery(id+"F0.wireOp",EDGE,"E197"),sQuery(id+"F0.wireOp",EDGE,"E198"),sQuery(id+"F0.wireOp",EDGE,"E199"),sQuery(id+"F0.wireOp",EDGE,"E200"),sQuery(id+"F0.wireOp",EDGE,"E201"),sQuery(id+"F0.wireOp",EDGE,"E202"),sQuery(id+"F0.wireOp",EDGE,"E203"),sQuery(id+"F0.wireOp",EDGE,"E204"),sQuery(id+"F0.wireOp",EDGE,"E205"),sQuery(id+"F0.wireOp",EDGE,"E206"),sQuery(id+"F0.wireOp",EDGE,"E207"),sQuery(id+"F0.wireOp",EDGE,"E208"),sQuery(id+"F0.wireOp",EDGE,"E209"),sQuery(id+"F0.wireOp",EDGE,"E210"),sQuery(id+"F0.wireOp",EDGE,"E211"),sQuery(id+"F0.wireOp",EDGE,"E212"),sQuery(id+"F0.wireOp",EDGE,"E213"),sQuery(id+"F0.wireOp",EDGE,"E214"),sQuery(id+"F0.wireOp",EDGE,"E215"),sQuery(id+"F0.wireOp",EDGE,"E216"),sQuery(id+"F0.wireOp",EDGE,"E217"),sQuery(id+"F0.wireOp",EDGE,"E218"),sQuery(id+"F0.wireOp",EDGE,"E219"),sQuery(id+"F0.wireOp",EDGE,"E220"),sQuery(id+"F0.wireOp",EDGE,"E221"),sQuery(id+"F0.wireOp",EDGE,"E222"),sQuery(id+"F0.wireOp",EDGE,"E223"),sQuery(id+"F0.wireOp",EDGE,"E224"),sQuery(id+"F0.wireOp",EDGE,"E225"),sQuery(id+"F0.wireOp",EDGE,"E226"),sQuery(id+"F0.wireOp",EDGE,"E227"),sQuery(id+"F0.wireOp",EDGE,"E228"),sQuery(id+"F0.wireOp",EDGE,"E229"),sQuery(id+"F0.wireOp",EDGE,"E230"),sQuery(id+"F0.wireOp",EDGE,"E231"),sQuery(id+"F0.wireOp",EDGE,"E232"),sQuery(id+"F0.wireOp",EDGE,"E233"),sQuery(id+"F0.wireOp",EDGE,"E234"),sQuery(id+"F0.wireOp",EDGE,"E235"),sQuery(id+"F0.wireOp",EDGE,"E236"),sQuery(id+"F0.wireOp",EDGE,"E237"),sQuery(id+"F0.wireOp",EDGE,"E238"),sQuery(id+"F0.wireOp",EDGE,"E239"),sQuery(id+"F0.wireOp",EDGE,"E240"),sQuery(id+"F0.wireOp",EDGE,"E241"),sQuery(id+"F0.wireOp",EDGE,"E242"),sQuery(id+"F0.wireOp",EDGE,"E243"),sQuery(id+"F0.wireOp",EDGE,"E244"),sQuery(id+"F0.wireOp",EDGE,"E245"),sQuery(id+"F0.wireOp",EDGE,"E246"),sQuery(id+"F0.wireOp",EDGE,"E247"),sQuery(id+"F0.wireOp",EDGE,"E248"),sQuery(id+"F0.wireOp",EDGE,"E249"),sQuery(id+"F0.wireOp",EDGE,"E250"),sQuery(id+"F0.wireOp",EDGE,"E251"),sQuery(id+"F0.wireOp",EDGE,"E252"),sQuery(id+"F0.wireOp",EDGE,"E253"),sQuery(id+"F0.wireOp",EDGE,"E254"),sQuery(id+"F0.wireOp",EDGE,"E255"),sQuery(id+"F0.wireOp",EDGE,"E256"),sQuery(id+"F0.wireOp",EDGE,"E257"),sQuery(id+"F0.wireOp",EDGE,"E258"),sQuery(id+"F0.wireOp",EDGE,"E259"),sQuery(id+"F0.wireOp",EDGE,"E260"),sQuery(id+"F0.wireOp",EDGE,"E261"),sQuery(id+"F0.wireOp",EDGE,"E262"),sQuery(id+"F0.wireOp",EDGE,"E263"),sQuery(id+"F0.wireOp",EDGE,"E264"),sQuery(id+"F0.wireOp",EDGE,"E265"),sQuery(id+"F0.wireOp",EDGE,"E266"),sQuery(id+"F0.wireOp",EDGE,"E267"),sQuery(id+"F0.wireOp",EDGE,"E268"),sQuery(id+"F0.wireOp",EDGE,"E269"),sQuery(id+"F0.wireOp",EDGE,"E270"),sQuery(id+"F0.wireOp",EDGE,"E271"),sQuery(id+"F0.wireOp",EDGE,"E272"),sQuery(id+"F0.wireOp",EDGE,"E273"),sQuery(id+"F0.wireOp",EDGE,"E274"),sQuery(id+"F0.wireOp",EDGE,"E275"),sQuery(id+"F0.wireOp",EDGE,"E276"),sQuery(id+"F0.wireOp",EDGE,"E277"),sQuery(id+"F0.wireOp",EDGE,"E278"),sQuery(id+"F0.wireOp",EDGE,"E279")])]});
            transform(context, id + "F9", {"entities" : qUnion([Q0]), "transformType" : TransformType.TRANSLATION_3D, "dx" : 0 * mm, "dy" : 0.8 * mm, "dz" : 0 * mm, "makeCopy" : false});
        }
        {
            var Q0;
            Q0=makeQuery(id+"F0.imprint","IMPRINT",FACE,{"disambiguationData":[TD([[makeQuery(id+"F0.imprint","IMPRINT",EDGE,{"derivedFrom":sQuery(id+"F0.wireOp",EDGE,"E76")}),-1.0]])]});
            extrude(context, id + "F10", {"entities" : qUnion([Q0]), "oppositeDirection" : true, "depth" : 1 * mm});
        }
        {
            var Q0;
            Q0=makeQuery(id+"F0.imprint","IMPRINT",FACE,{"disambiguationData":[TD([[makeQuery(id+"F0.imprint","IMPRINT",EDGE,{"derivedFrom":sQuery(id+"F0.wireOp",EDGE,"E356")}),-1.0]])]});
            extrude(context, id + "F11", {"entities" : qUnion([Q0]), "oppositeDirection" : true, "depth" : 1 * mm});
        }
        {
            var Q0;
            Q0=makeQuery(id+"F0.imprint","IMPRINT",FACE,{"disambiguationData":[TD([[makeQuery(id+"F0.imprint","IMPRINT",EDGE,{"derivedFrom":sQuery(id+"F0.wireOp",EDGE,"E636")}),-1.0]])]});
            extrude(context, id + "F12", {"entities" : qUnion([Q0]), "operationType" : NewBodyOperationType.ADD, "oppositeDirection" : true, "depth" : 1 * mm});
        }
        {
            var Q0;
            Q0=makeQuery(id+"F0.imprint","IMPRINT",FACE,{"disambiguationData":[TD([[makeQuery(id+"F0.imprint","IMPRINT",EDGE,{"derivedFrom":sQuery(id+"F0.wireOp",EDGE,"E496")}),-1.0]])]});
            extrude(context, id + "F13", {"entities" : qUnion([Q0]), "oppositeDirection" : true, "depth" : 1 * mm});
        }
        {
            var Q0;
            Q0=makeQuery(id+"F0.imprint","IMPRINT",FACE,{"disambiguationData":[TD([[makeQuery(id+"F0.imprint","IMPRINT",EDGE,{"derivedFrom":sQuery(id+"F0.wireOp",EDGE,"E232")}),-1.0]])]});
            extrude(context, id + "F14", {"entities" : qUnion([Q0]), "oppositeDirection" : true, "depth" : 1 * mm});
        }
        {
            var Q0;
            Q0=makeQuery(id+"F0.imprint","IMPRINT",FACE,{"disambiguationData":[TD([[makeQuery(id+"F0.imprint","IMPRINT",EDGE,{"derivedFrom":sQuery(id+"F0.wireOp",EDGE,"E256")}),-1.0]])]});
            var Q1;
            Q1=makeQuery(id+"F0.imprint","IMPRINT",FACE,{"disambiguationData":[TD([[makeQuery(id+"F0.imprint","IMPRINT",EDGE,{"derivedFrom":sQuery(id+"F0.wireOp",EDGE,"E380")}),-1.0]])]});
            var Q2;
            Q2=makeQuery(id+"F0.imprint","IMPRINT",FACE,{"disambiguationData":[TD([[makeQuery(id+"F0.imprint","IMPRINT",EDGE,{"derivedFrom":sQuery(id+"F0.wireOp",EDGE,"E520")}),-1.0]])]});
            var Q3;
            Q3=makeQuery(id+"F0.imprint","IMPRINT",FACE,{"disambiguationData":[TD([[makeQuery(id+"F0.imprint","IMPRINT",EDGE,{"derivedFrom":sQuery(id+"F0.wireOp",EDGE,"E660")}),-1.0]])]});
            var Q4;
            Q4=makeQuery(id+"F0.imprint","IMPRINT",FACE,{"disambiguationData":[TD([[makeQuery(id+"F0.imprint","IMPRINT",EDGE,{"derivedFrom":sQuery(id+"F0.wireOp",EDGE,"E116")}),-1.0]])]});
            extrude(context, id + "F15", {"entities" : qUnion([Q0, Q1, Q2, Q3, Q4]), "operationType" : NewBodyOperationType.ADD, "oppositeDirection" : true, "depth" : 1.2 * mm});
        }
    });
